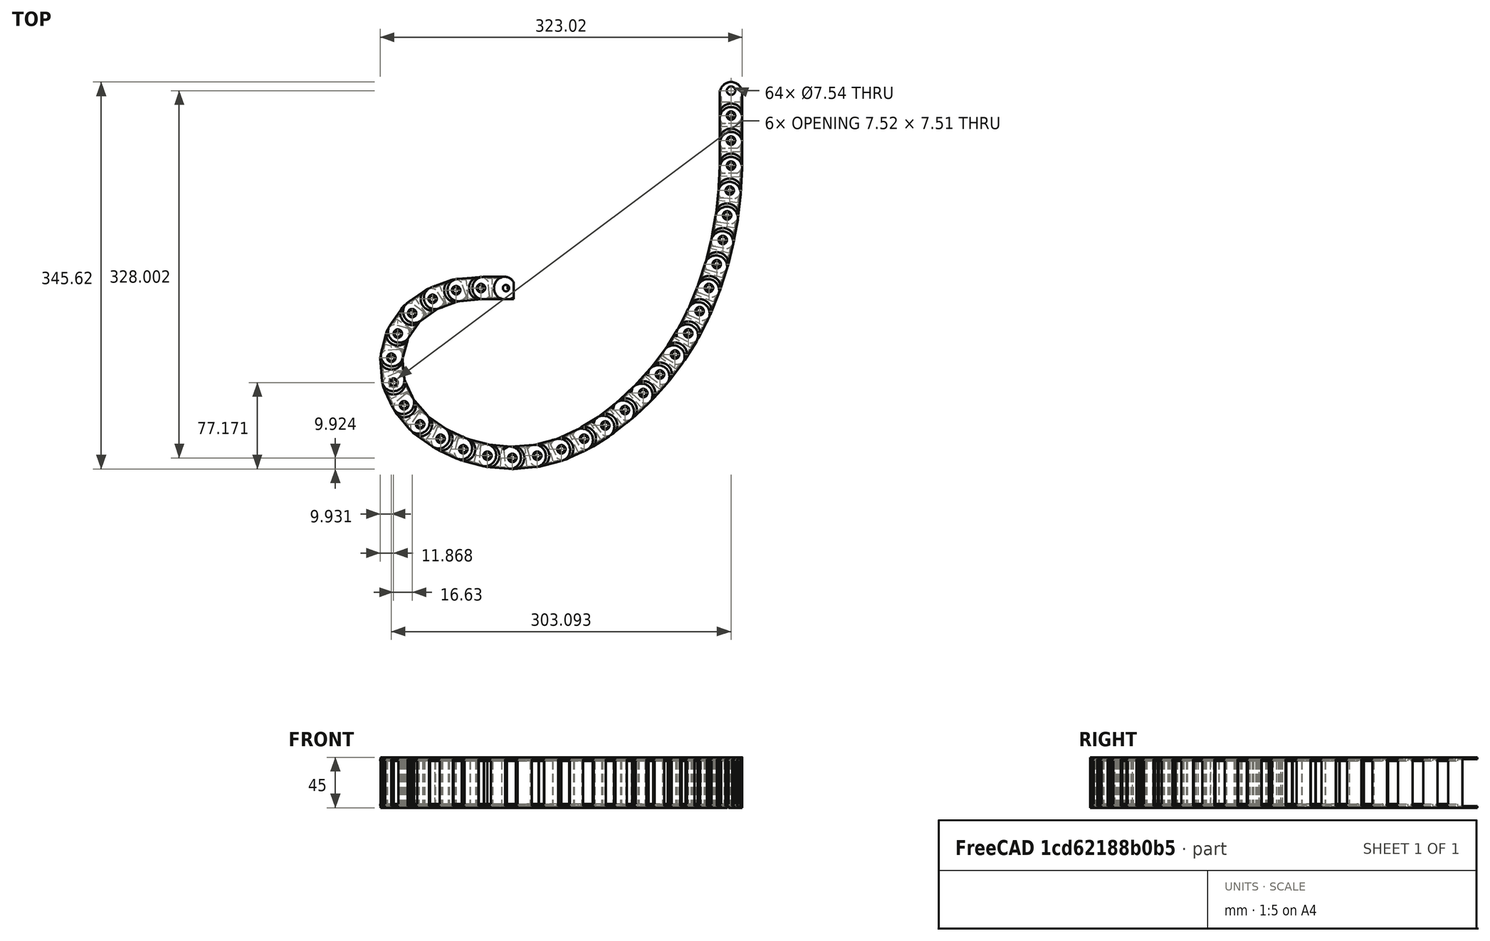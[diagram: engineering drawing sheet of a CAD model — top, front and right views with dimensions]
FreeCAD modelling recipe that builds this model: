
FCSTD DOCUMENT  (FreeCAD 0.16R4945 (Git))
Label: XY-Chain
License: CreativeCommons Attribution-ShareAlike
LicenseURL: http://creativecommons.org/licenses/by-sa/4.0/
objects: Part::Box×320, Part::Cylinder×224, Part::Cut×160, Part::MultiFuse×129, Part::Fuse×96, Part::FeaturePython×1
note: 930 computed .brp shape members not serialized (recipe doc carries the construction recipe); baked Part::Feature solids carry a one-line shape summary decoded from their .brp

FEATURE [Part::Box] cube
  Height = 20
  Length = 26.9231
  Placement = pos=(0,0.1,0) rot=(0,0,1;0rad)
  Width = 45
FEATURE [Part::Cylinder] cylinder
  Angle = 360
  Height = 45
  Placement = pos=(26.9231,0.1,10) rot=(-1,0,0;1.5708rad)
  Radius = 10
FEATURE [Part::Fuse] union
  Base = -> cube
  Tool = -> cylinder
FEATURE [Part::Cylinder] cylinder001
  Angle = 360
  Height = 3
  Placement = pos=(7.07692,2,10) rot=(1,0,0;1.5708rad)
  Radius = 10.5385
FEATURE [Part::Cylinder] cylinder002
  Angle = 360
  Height = 45.9
  Placement = pos=(29.2308,45.5,10) rot=(1,0,0;1.5708rad)
  Radius = 3.76923
FEATURE [Part::Cylinder] cylinder003
  Angle = 360
  Height = 3
  Placement = pos=(7.07692,46.3,10) rot=(1,0,0;1.5708rad)
  Radius = 10.5385
FEATURE [Part::MultiFuse] union001
  Shapes = -> [cylinder001,cylinder002,cylinder003]
FEATURE [Part::Box] cube001
  Height = 6.15385
  Length = 7.69231
  Placement = pos=(0,-0.5,0) rot=(0,0,1;0rad)
  Width = 45.9
FEATURE [Part::Cylinder] cylinder004
  Angle = 360
  Height = 45.9
  Placement = pos=(7.69231,45.4,8.46154) rot=(1,0,0;1.5708rad)
  Radius = 8.46154
FEATURE [Part::Cut] difference
  Base = -> cube001
  Tool = -> cylinder004
FEATURE [Part::Box] cube002
  Height = 6.15385
  Length = 7.69231
  Placement = pos=(0,-0.5,9) rot=(0,0,1;0rad)
  Width = 45.9
FEATURE [Part::Cylinder] cylinder005
  Angle = 360
  Height = 45.9
  Placement = pos=(7.69231,45.4,11.5385) rot=(1,0,0;1.5708rad)
  Radius = 8.46154
FEATURE [Part::Cut] difference001
  Base = -> cube002
  Tool = -> cylinder005
FEATURE [Part::MultiFuse] union002
  Shapes = -> [union001,difference,difference001]
FEATURE [Part::Cut] difference002
  Base = -> union
  Tool = -> union002
FEATURE [Part::Cylinder] cylinder006
  Angle = 360
  Height = 44.2
  Placement = pos=(6.92308,44.7,10) rot=(1,0,0;1.5708rad)
  Radius = 2.84615
FEATURE [Part::Box] cube003
  Height = 4
  Length = 4
  Placement = pos=(0.538462,-2,6.92308) rot=(0,0,-1;0.349066rad)
  Width = 4
FEATURE [Part::Box] cube004
  Height = 4
  Length = 4
  Placement = pos=(0.538462,18.8,6.92308) rot=(0,0,-1;1.22173rad)
  Width = 4
FEATURE [Part::Fuse] union003
  Base = -> cube003
  Tool = -> cube004
FEATURE [Part::Cut] difference003
  Base = -> cylinder006
  Tool = -> union003
FEATURE [Part::Fuse] union004
  Base = -> difference002
  Tool = -> difference003
FEATURE [Part::Box] cube005
  Height = 17
  Length = 40
  Placement = pos=(-1.53846,3.4,1.5) rot=(0,0,1;0rad)
  Width = 38.4
FEATURE [Part::Box] cube006
  Height = 15.3846
  Length = 12.3077
  Placement = pos=(23.6154,3.4,5.38462) rot=(0,0,1;0rad)
  Width = 38.4
FEATURE [Part::Box] cube007
  Height = 24.6154
  Length = 12.3077
  Placement = pos=(-1.53846,3.4,-2.30769) rot=(0,0,1;0rad)
  Width = 38.4
FEATURE [Part::Box] cube008
  Height = 17
  Length = 9.23077
  Placement = pos=(19.2308,1.6,1.5) rot=(0,0,1;0rad)
  Width = 42
FEATURE [Part::Box] cube009
  Height = 20
  Length = 15.3846
  Placement = pos=(23.6154,1.6,0) rot=(0,0,1;0rad)
  Width = 42
FEATURE [Part::MultiFuse] Group
  Shapes = -> [cube007,cube008,cube009]
FEATURE [Part::MultiFuse] union005
  Shapes = -> [cube005,cube006,Group]
FEATURE [Part::Cut] difference004
  Base = -> union004
  Placement = pos=(214.009,254.444,566) rot=(0,-0.707107,0.707107;3.14159rad)
  Tool = -> union005
FEATURE [Part::Box] cube010
  Height = 20
  Length = 26.9231
  Placement = pos=(0,0.1,0) rot=(0,0,1;0rad)
  Width = 45
FEATURE [Part::Cylinder] cylinder007
  Angle = 360
  Height = 45
  Placement = pos=(26.9231,0.1,10) rot=(-1,0,0;1.5708rad)
  Radius = 10
FEATURE [Part::Fuse] union006
  Base = -> cube010
  Tool = -> cylinder007
FEATURE [Part::Cylinder] cylinder008
  Angle = 360
  Height = 3
  Placement = pos=(7.07692,2,10) rot=(1,0,0;1.5708rad)
  Radius = 10.5385
FEATURE [Part::Cylinder] cylinder009
  Angle = 360
  Height = 45.9
  Placement = pos=(29.2308,45.5,10) rot=(1,0,0;1.5708rad)
  Radius = 3.76923
FEATURE [Part::Cylinder] cylinder010
  Angle = 360
  Height = 3
  Placement = pos=(7.07692,46.3,10) rot=(1,0,0;1.5708rad)
  Radius = 10.5385
FEATURE [Part::MultiFuse] union007
  Shapes = -> [cylinder008,cylinder009,cylinder010]
FEATURE [Part::Box] cube011
  Height = 6.15385
  Length = 7.69231
  Placement = pos=(0,-0.5,0) rot=(0,0,1;0rad)
  Width = 45.9
FEATURE [Part::Cylinder] cylinder011
  Angle = 360
  Height = 45.9
  Placement = pos=(7.69231,45.4,8.46154) rot=(1,0,0;1.5708rad)
  Radius = 8.46154
FEATURE [Part::Cut] difference005
  Base = -> cube011
  Tool = -> cylinder011
FEATURE [Part::Box] cube012
  Height = 6.15385
  Length = 7.69231
  Placement = pos=(0,-0.5,9) rot=(0,0,1;0rad)
  Width = 45.9
FEATURE [Part::Cylinder] cylinder012
  Angle = 360
  Height = 45.9
  Placement = pos=(7.69231,45.4,11.5385) rot=(1,0,0;1.5708rad)
  Radius = 8.46154
FEATURE [Part::Cut] difference006
  Base = -> cube012
  Tool = -> cylinder012
FEATURE [Part::MultiFuse] union008
  Shapes = -> [union007,difference005,difference006]
FEATURE [Part::Cut] difference007
  Base = -> union006
  Tool = -> union008
FEATURE [Part::Cylinder] cylinder013
  Angle = 360
  Height = 44.2
  Placement = pos=(6.92308,44.7,10) rot=(1,0,0;1.5708rad)
  Radius = 2.84615
FEATURE [Part::Box] cube013
  Height = 4
  Length = 4
  Placement = pos=(0.538462,-2,6.92308) rot=(0,0,-1;0.349066rad)
  Width = 4
FEATURE [Part::Box] cube014
  Height = 4
  Length = 4
  Placement = pos=(0.538462,18.8,6.92308) rot=(0,0,-1;1.22173rad)
  Width = 4
FEATURE [Part::Fuse] union009
  Base = -> cube013
  Tool = -> cube014
FEATURE [Part::Cut] difference008
  Base = -> cylinder013
  Tool = -> union009
FEATURE [Part::Fuse] union010
  Base = -> difference007
  Tool = -> difference008
FEATURE [Part::Box] cube015
  Height = 17
  Length = 40
  Placement = pos=(-1.53846,3.4,1.5) rot=(0,0,1;0rad)
  Width = 38.4
FEATURE [Part::Box] cube016
  Height = 15.3846
  Length = 12.3077
  Placement = pos=(23.6154,3.4,5.38462) rot=(0,0,1;0rad)
  Width = 38.4
FEATURE [Part::Box] cube017
  Height = 24.6154
  Length = 12.3077
  Placement = pos=(-1.53846,3.4,-2.30769) rot=(0,0,1;0rad)
  Width = 38.4
FEATURE [Part::Box] cube018
  Height = 17
  Length = 9.23077
  Placement = pos=(19.2308,1.6,1.5) rot=(0,0,1;0rad)
  Width = 42
FEATURE [Part::Box] cube019
  Height = 20
  Length = 15.3846
  Placement = pos=(23.6154,1.6,0) rot=(0,0,1;0rad)
  Width = 42
FEATURE [Part::MultiFuse] Group001
  Shapes = -> [cube017,cube018,cube019]
FEATURE [Part::MultiFuse] union011
  Shapes = -> [cube015,cube016,Group001]
FEATURE [Part::Cut] difference009
  Base = -> union010
  Placement = pos=(190.804,255.009,566) rot=(0.030858,-0.70677,0.70677;3.20329rad)
  Tool = -> union011
FEATURE [Part::Box] cube020
  Height = 20
  Length = 26.9231
  Placement = pos=(0,0.1,0) rot=(0,0,1;0rad)
  Width = 45
FEATURE [Part::Cylinder] cylinder014
  Angle = 360
  Height = 45
  Placement = pos=(26.9231,0.1,10) rot=(-1,0,0;1.5708rad)
  Radius = 10
FEATURE [Part::Fuse] union012
  Base = -> cube020
  Tool = -> cylinder014
FEATURE [Part::Cylinder] cylinder015
  Angle = 360
  Height = 3
  Placement = pos=(7.07692,2,10) rot=(1,0,0;1.5708rad)
  Radius = 10.5385
FEATURE [Part::Cylinder] cylinder016
  Angle = 360
  Height = 45.9
  Placement = pos=(29.2308,45.5,10) rot=(1,0,0;1.5708rad)
  Radius = 3.76923
FEATURE [Part::Cylinder] cylinder017
  Angle = 360
  Height = 3
  Placement = pos=(7.07692,46.3,10) rot=(1,0,0;1.5708rad)
  Radius = 10.5385
FEATURE [Part::MultiFuse] union013
  Shapes = -> [cylinder015,cylinder016,cylinder017]
FEATURE [Part::Box] cube021
  Height = 6.15385
  Length = 7.69231
  Placement = pos=(0,-0.5,0) rot=(0,0,1;0rad)
  Width = 45.9
FEATURE [Part::Cylinder] cylinder018
  Angle = 360
  Height = 45.9
  Placement = pos=(7.69231,45.4,8.46154) rot=(1,0,0;1.5708rad)
  Radius = 8.46154
FEATURE [Part::Cut] difference010
  Base = -> cube021
  Tool = -> cylinder018
FEATURE [Part::Box] cube022
  Height = 6.15385
  Length = 7.69231
  Placement = pos=(0,-0.5,9) rot=(0,0,1;0rad)
  Width = 45.9
FEATURE [Part::Cylinder] cylinder019
  Angle = 360
  Height = 45.9
  Placement = pos=(7.69231,45.4,11.5385) rot=(1,0,0;1.5708rad)
  Radius = 8.46154
FEATURE [Part::Cut] difference011
  Base = -> cube022
  Tool = -> cylinder019
FEATURE [Part::MultiFuse] union014
  Shapes = -> [union013,difference010,difference011]
FEATURE [Part::Cut] difference012
  Base = -> union012
  Tool = -> union014
FEATURE [Part::Cylinder] cylinder020
  Angle = 360
  Height = 44.2
  Placement = pos=(6.92308,44.7,10) rot=(1,0,0;1.5708rad)
  Radius = 2.84615
FEATURE [Part::Box] cube023
  Height = 4
  Length = 4
  Placement = pos=(0.538462,-2,6.92308) rot=(0,0,-1;0.349066rad)
  Width = 4
FEATURE [Part::Box] cube024
  Height = 4
  Length = 4
  Placement = pos=(0.538462,18.8,6.92308) rot=(0,0,-1;1.22173rad)
  Width = 4
FEATURE [Part::Fuse] union015
  Base = -> cube023
  Tool = -> cube024
FEATURE [Part::Cut] difference013
  Base = -> cylinder020
  Tool = -> union015
FEATURE [Part::Fuse] union016
  Base = -> difference012
  Tool = -> difference013
FEATURE [Part::Box] cube025
  Height = 17
  Length = 40
  Placement = pos=(-1.53846,3.4,1.5) rot=(0,0,1;0rad)
  Width = 38.4
FEATURE [Part::Box] cube026
  Height = 15.3846
  Length = 12.3077
  Placement = pos=(23.6154,3.4,5.38462) rot=(0,0,1;0rad)
  Width = 38.4
FEATURE [Part::Box] cube027
  Height = 24.6154
  Length = 12.3077
  Placement = pos=(-1.53846,3.4,-2.30769) rot=(0,0,1;0rad)
  Width = 38.4
FEATURE [Part::Box] cube028
  Height = 17
  Length = 9.23077
  Placement = pos=(19.2308,1.6,1.5) rot=(0,0,1;0rad)
  Width = 42
FEATURE [Part::Box] cube029
  Height = 20
  Length = 15.3846
  Placement = pos=(23.6154,1.6,0) rot=(0,0,1;0rad)
  Width = 42
FEATURE [Part::MultiFuse] Group002
  Shapes = -> [cube027,cube028,cube029]
FEATURE [Part::MultiFuse] union017
  Shapes = -> [cube025,cube026,Group002]
FEATURE [Part::Cut] difference014
  Base = -> union016
  Placement = pos=(165.641,254.265,566) rot=(0.123724,-0.701674,0.701674;3.38779rad)
  Tool = -> union017
FEATURE [Part::Box] cube030
  Height = 20
  Length = 26.9231
  Placement = pos=(0,0.1,0) rot=(0,0,1;0rad)
  Width = 45
FEATURE [Part::Cylinder] cylinder021
  Angle = 360
  Height = 45
  Placement = pos=(26.9231,0.1,10) rot=(-1,0,0;1.5708rad)
  Radius = 10
FEATURE [Part::Fuse] union018
  Base = -> cube030
  Tool = -> cylinder021
FEATURE [Part::Cylinder] cylinder022
  Angle = 360
  Height = 3
  Placement = pos=(7.07692,2,10) rot=(1,0,0;1.5708rad)
  Radius = 10.5385
FEATURE [Part::Cylinder] cylinder023
  Angle = 360
  Height = 45.9
  Placement = pos=(29.2308,45.5,10) rot=(1,0,0;1.5708rad)
  Radius = 3.76923
FEATURE [Part::Cylinder] cylinder024
  Angle = 360
  Height = 3
  Placement = pos=(7.07692,46.3,10) rot=(1,0,0;1.5708rad)
  Radius = 10.5385
FEATURE [Part::MultiFuse] union019
  Shapes = -> [cylinder022,cylinder023,cylinder024]
FEATURE [Part::Box] cube031
  Height = 6.15385
  Length = 7.69231
  Placement = pos=(0,-0.5,0) rot=(0,0,1;0rad)
  Width = 45.9
FEATURE [Part::Cylinder] cylinder025
  Angle = 360
  Height = 45.9
  Placement = pos=(7.69231,45.4,8.46154) rot=(1,0,0;1.5708rad)
  Radius = 8.46154
FEATURE [Part::Cut] difference015
  Base = -> cube031
  Tool = -> cylinder025
FEATURE [Part::Box] cube032
  Height = 6.15385
  Length = 7.69231
  Placement = pos=(0,-0.5,9) rot=(0,0,1;0rad)
  Width = 45.9
FEATURE [Part::Cylinder] cylinder026
  Angle = 360
  Height = 45.9
  Placement = pos=(7.69231,45.4,11.5385) rot=(1,0,0;1.5708rad)
  Radius = 8.46154
FEATURE [Part::Cut] difference016
  Base = -> cube032
  Tool = -> cylinder026
FEATURE [Part::MultiFuse] union020
  Shapes = -> [union019,difference015,difference016]
FEATURE [Part::Cut] difference017
  Base = -> union018
  Tool = -> union020
FEATURE [Part::Cylinder] cylinder027
  Angle = 360
  Height = 44.2
  Placement = pos=(6.92308,44.7,10) rot=(1,0,0;1.5708rad)
  Radius = 2.84615
FEATURE [Part::Box] cube033
  Height = 4
  Length = 4
  Placement = pos=(0.538462,-2,6.92308) rot=(0,0,-1;0.349066rad)
  Width = 4
FEATURE [Part::Box] cube034
  Height = 4
  Length = 4
  Placement = pos=(0.538462,18.8,6.92308) rot=(0,0,-1;1.22173rad)
  Width = 4
FEATURE [Part::Fuse] union021
  Base = -> cube033
  Tool = -> cube034
FEATURE [Part::Cut] difference018
  Base = -> cylinder027
  Tool = -> union021
FEATURE [Part::Fuse] union022
  Base = -> difference017
  Tool = -> difference018
FEATURE [Part::Box] cube035
  Height = 17
  Length = 40
  Placement = pos=(-1.53846,3.4,1.5) rot=(0,0,1;0rad)
  Width = 38.4
FEATURE [Part::Box] cube036
  Height = 15.3846
  Length = 12.3077
  Placement = pos=(23.6154,3.4,5.38462) rot=(0,0,1;0rad)
  Width = 38.4
FEATURE [Part::Box] cube037
  Height = 24.6154
  Length = 12.3077
  Placement = pos=(-1.53846,3.4,-2.30769) rot=(0,0,1;0rad)
  Width = 38.4
FEATURE [Part::Box] cube038
  Height = 17
  Length = 9.23077
  Placement = pos=(19.2308,1.6,1.5) rot=(0,0,1;0rad)
  Width = 42
FEATURE [Part::Box] cube039
  Height = 20
  Length = 15.3846
  Placement = pos=(23.6154,1.6,0) rot=(0,0,1;0rad)
  Width = 42
FEATURE [Part::MultiFuse] Group003
  Shapes = -> [cube037,cube038,cube039]
FEATURE [Part::MultiFuse] union023
  Shapes = -> [cube035,cube036,Group003]
FEATURE [Part::Cut] difference019
  Base = -> union022
  Placement = pos=(141.529,247.033,566) rot=(0.217607,-0.690162,0.690162;3.57013rad)
  Tool = -> union023
FEATURE [Part::Box] cube040
  Height = 20
  Length = 26.9231
  Placement = pos=(0,0.1,0) rot=(0,0,1;0rad)
  Width = 45
FEATURE [Part::Cylinder] cylinder028
  Angle = 360
  Height = 45
  Placement = pos=(26.9231,0.1,10) rot=(-1,0,0;1.5708rad)
  Radius = 10
FEATURE [Part::Fuse] union024
  Base = -> cube040
  Tool = -> cylinder028
FEATURE [Part::Cylinder] cylinder029
  Angle = 360
  Height = 3
  Placement = pos=(7.07692,2,10) rot=(1,0,0;1.5708rad)
  Radius = 10.5385
FEATURE [Part::Cylinder] cylinder030
  Angle = 360
  Height = 45.9
  Placement = pos=(29.2308,45.5,10) rot=(1,0,0;1.5708rad)
  Radius = 3.76923
FEATURE [Part::Cylinder] cylinder031
  Angle = 360
  Height = 3
  Placement = pos=(7.07692,46.3,10) rot=(1,0,0;1.5708rad)
  Radius = 10.5385
FEATURE [Part::MultiFuse] union025
  Shapes = -> [cylinder029,cylinder030,cylinder031]
FEATURE [Part::Box] cube041
  Height = 6.15385
  Length = 7.69231
  Placement = pos=(0,-0.5,0) rot=(0,0,1;0rad)
  Width = 45.9
FEATURE [Part::Cylinder] cylinder032
  Angle = 360
  Height = 45.9
  Placement = pos=(7.69231,45.4,8.46154) rot=(1,0,0;1.5708rad)
  Radius = 8.46154
FEATURE [Part::Cut] difference020
  Base = -> cube041
  Tool = -> cylinder032
FEATURE [Part::Box] cube042
  Height = 6.15385
  Length = 7.69231
  Placement = pos=(0,-0.5,9) rot=(0,0,1;0rad)
  Width = 45.9
FEATURE [Part::Cylinder] cylinder033
  Angle = 360
  Height = 45.9
  Placement = pos=(7.69231,45.4,11.5385) rot=(1,0,0;1.5708rad)
  Radius = 8.46154
FEATURE [Part::Cut] difference021
  Base = -> cube042
  Tool = -> cylinder033
FEATURE [Part::MultiFuse] union026
  Shapes = -> [union025,difference020,difference021]
FEATURE [Part::Cut] difference022
  Base = -> union024
  Tool = -> union026
FEATURE [Part::Cylinder] cylinder034
  Angle = 360
  Height = 44.2
  Placement = pos=(6.92308,44.7,10) rot=(1,0,0;1.5708rad)
  Radius = 2.84615
FEATURE [Part::Box] cube043
  Height = 4
  Length = 4
  Placement = pos=(0.538462,-2,6.92308) rot=(0,0,-1;0.349066rad)
  Width = 4
FEATURE [Part::Box] cube044
  Height = 4
  Length = 4
  Placement = pos=(0.538462,18.8,6.92308) rot=(0,0,-1;1.22173rad)
  Width = 4
FEATURE [Part::Fuse] union027
  Base = -> cube043
  Tool = -> cube044
FEATURE [Part::Cut] difference023
  Base = -> cylinder034
  Tool = -> union027
FEATURE [Part::Fuse] union028
  Base = -> difference022
  Tool = -> difference023
FEATURE [Part::Box] cube045
  Height = 17
  Length = 40
  Placement = pos=(-1.53846,3.4,1.5) rot=(0,0,1;0rad)
  Width = 38.4
FEATURE [Part::Box] cube046
  Height = 15.3846
  Length = 12.3077
  Placement = pos=(23.6154,3.4,5.38462) rot=(0,0,1;0rad)
  Width = 38.4
FEATURE [Part::Box] cube047
  Height = 24.6154
  Length = 12.3077
  Placement = pos=(-1.53846,3.4,-2.30769) rot=(0,0,1;0rad)
  Width = 38.4
FEATURE [Part::Box] cube048
  Height = 17
  Length = 9.23077
  Placement = pos=(19.2308,1.6,1.5) rot=(0,0,1;0rad)
  Width = 42
FEATURE [Part::Box] cube049
  Height = 20
  Length = 15.3846
  Placement = pos=(23.6154,1.6,0) rot=(0,0,1;0rad)
  Width = 42
FEATURE [Part::MultiFuse] Group004
  Shapes = -> [cube047,cube048,cube049]
FEATURE [Part::MultiFuse] union029
  Shapes = -> [cube045,cube046,Group004]
FEATURE [Part::Cut] difference024
  Base = -> union028
  Placement = pos=(119.099,233.482,566) rot=(0.345437,-0.663579,0.663579;3.8068rad)
  Tool = -> union029
FEATURE [Part::Box] cube050
  Height = 20
  Length = 26.9231
  Placement = pos=(0,0.1,0) rot=(0,0,1;0rad)
  Width = 45
FEATURE [Part::Cylinder] cylinder035
  Angle = 360
  Height = 45
  Placement = pos=(26.9231,0.1,10) rot=(-1,0,0;1.5708rad)
  Radius = 10
FEATURE [Part::Fuse] union030
  Base = -> cube050
  Tool = -> cylinder035
FEATURE [Part::Cylinder] cylinder036
  Angle = 360
  Height = 3
  Placement = pos=(7.07692,2,10) rot=(1,0,0;1.5708rad)
  Radius = 10.5385
FEATURE [Part::Cylinder] cylinder037
  Angle = 360
  Height = 45.9
  Placement = pos=(29.2308,45.5,10) rot=(1,0,0;1.5708rad)
  Radius = 3.76923
FEATURE [Part::Cylinder] cylinder038
  Angle = 360
  Height = 3
  Placement = pos=(7.07692,46.3,10) rot=(1,0,0;1.5708rad)
  Radius = 10.5385
FEATURE [Part::MultiFuse] union031
  Shapes = -> [cylinder036,cylinder037,cylinder038]
FEATURE [Part::Box] cube051
  Height = 6.15385
  Length = 7.69231
  Placement = pos=(0,-0.5,0) rot=(0,0,1;0rad)
  Width = 45.9
FEATURE [Part::Cylinder] cylinder039
  Angle = 360
  Height = 45.9
  Placement = pos=(7.69231,45.4,8.46154) rot=(1,0,0;1.5708rad)
  Radius = 8.46154
FEATURE [Part::Cut] difference025
  Base = -> cube051
  Tool = -> cylinder039
FEATURE [Part::Box] cube052
  Height = 6.15385
  Length = 7.69231
  Placement = pos=(0,-0.5,9) rot=(0,0,1;0rad)
  Width = 45.9
FEATURE [Part::Cylinder] cylinder040
  Angle = 360
  Height = 45.9
  Placement = pos=(7.69231,45.4,11.5385) rot=(1,0,0;1.5708rad)
  Radius = 8.46154
FEATURE [Part::Cut] difference026
  Base = -> cube052
  Tool = -> cylinder040
FEATURE [Part::MultiFuse] union032
  Shapes = -> [union031,difference025,difference026]
FEATURE [Part::Cut] difference027
  Base = -> union030
  Tool = -> union032
FEATURE [Part::Cylinder] cylinder041
  Angle = 360
  Height = 44.2
  Placement = pos=(6.92308,44.7,10) rot=(1,0,0;1.5708rad)
  Radius = 2.84615
FEATURE [Part::Box] cube053
  Height = 4
  Length = 4
  Placement = pos=(0.538462,-2,6.92308) rot=(0,0,-1;0.349066rad)
  Width = 4
FEATURE [Part::Box] cube054
  Height = 4
  Length = 4
  Placement = pos=(0.538462,18.8,6.92308) rot=(0,0,-1;1.22173rad)
  Width = 4
FEATURE [Part::Fuse] union033
  Base = -> cube053
  Tool = -> cube054
FEATURE [Part::Cut] difference028
  Base = -> cylinder041
  Tool = -> union033
FEATURE [Part::Fuse] union034
  Base = -> difference027
  Tool = -> difference028
FEATURE [Part::Box] cube055
  Height = 17
  Length = 40
  Placement = pos=(-1.53846,3.4,1.5) rot=(0,0,1;0rad)
  Width = 38.4
FEATURE [Part::Box] cube056
  Height = 15.3846
  Length = 12.3077
  Placement = pos=(23.6154,3.4,5.38462) rot=(0,0,1;0rad)
  Width = 38.4
FEATURE [Part::Box] cube057
  Height = 24.6154
  Length = 12.3077
  Placement = pos=(-1.53846,3.4,-2.30769) rot=(0,0,1;0rad)
  Width = 38.4
FEATURE [Part::Box] cube058
  Height = 17
  Length = 9.23077
  Placement = pos=(19.2308,1.6,1.5) rot=(0,0,1;0rad)
  Width = 42
FEATURE [Part::Box] cube059
  Height = 20
  Length = 15.3846
  Placement = pos=(23.6154,1.6,0) rot=(0,0,1;0rad)
  Width = 42
FEATURE [Part::MultiFuse] Group005
  Shapes = -> [cube057,cube058,cube059]
FEATURE [Part::MultiFuse] union035
  Shapes = -> [cube055,cube056,Group005]
FEATURE [Part::Cut] difference029
  Base = -> union034
  Placement = pos=(102.657,213.077,566) rot=(0.476905,-0.621515,0.621515;4.0316rad)
  Tool = -> union035
FEATURE [Part::Box] cube060
  Height = 20
  Length = 26.9231
  Placement = pos=(0,0.1,0) rot=(0,0,1;0rad)
  Width = 45
FEATURE [Part::Cylinder] cylinder042
  Angle = 360
  Height = 45
  Placement = pos=(26.9231,0.1,10) rot=(-1,0,0;1.5708rad)
  Radius = 10
FEATURE [Part::Fuse] union036
  Base = -> cube060
  Tool = -> cylinder042
FEATURE [Part::Cylinder] cylinder043
  Angle = 360
  Height = 3
  Placement = pos=(7.07692,2,10) rot=(1,0,0;1.5708rad)
  Radius = 10.5385
FEATURE [Part::Cylinder] cylinder044
  Angle = 360
  Height = 45.9
  Placement = pos=(29.2308,45.5,10) rot=(1,0,0;1.5708rad)
  Radius = 3.76923
FEATURE [Part::Cylinder] cylinder045
  Angle = 360
  Height = 3
  Placement = pos=(7.07692,46.3,10) rot=(1,0,0;1.5708rad)
  Radius = 10.5385
FEATURE [Part::MultiFuse] union037
  Shapes = -> [cylinder043,cylinder044,cylinder045]
FEATURE [Part::Box] cube061
  Height = 6.15385
  Length = 7.69231
  Placement = pos=(0,-0.5,0) rot=(0,0,1;0rad)
  Width = 45.9
FEATURE [Part::Cylinder] cylinder046
  Angle = 360
  Height = 45.9
  Placement = pos=(7.69231,45.4,8.46154) rot=(1,0,0;1.5708rad)
  Radius = 8.46154
FEATURE [Part::Cut] difference030
  Base = -> cube061
  Tool = -> cylinder046
FEATURE [Part::Box] cube062
  Height = 6.15385
  Length = 7.69231
  Placement = pos=(0,-0.5,9) rot=(0,0,1;0rad)
  Width = 45.9
FEATURE [Part::Cylinder] cylinder047
  Angle = 360
  Height = 45.9
  Placement = pos=(7.69231,45.4,11.5385) rot=(1,0,0;1.5708rad)
  Radius = 8.46154
FEATURE [Part::Cut] difference031
  Base = -> cube062
  Tool = -> cylinder047
FEATURE [Part::MultiFuse] union038
  Shapes = -> [union037,difference030,difference031]
FEATURE [Part::Cut] difference032
  Base = -> union036
  Tool = -> union038
FEATURE [Part::Cylinder] cylinder048
  Angle = 360
  Height = 44.2
  Placement = pos=(6.92308,44.7,10) rot=(1,0,0;1.5708rad)
  Radius = 2.84615
FEATURE [Part::Box] cube063
  Height = 4
  Length = 4
  Placement = pos=(0.538462,-2,6.92308) rot=(0,0,-1;0.349066rad)
  Width = 4
FEATURE [Part::Box] cube064
  Height = 4
  Length = 4
  Placement = pos=(0.538462,18.8,6.92308) rot=(0,0,-1;1.22173rad)
  Width = 4
FEATURE [Part::Fuse] union039
  Base = -> cube063
  Tool = -> cube064
FEATURE [Part::Cut] difference033
  Base = -> cylinder048
  Tool = -> union039
FEATURE [Part::Fuse] union040
  Base = -> difference032
  Tool = -> difference033
FEATURE [Part::Box] cube065
  Height = 17
  Length = 40
  Placement = pos=(-1.53846,3.4,1.5) rot=(0,0,1;0rad)
  Width = 38.4
FEATURE [Part::Box] cube066
  Height = 15.3846
  Length = 12.3077
  Placement = pos=(23.6154,3.4,5.38462) rot=(0,0,1;0rad)
  Width = 38.4
FEATURE [Part::Box] cube067
  Height = 24.6154
  Length = 12.3077
  Placement = pos=(-1.53846,3.4,-2.30769) rot=(0,0,1;0rad)
  Width = 38.4
FEATURE [Part::Box] cube068
  Height = 17
  Length = 9.23077
  Placement = pos=(19.2308,1.6,1.5) rot=(0,0,1;0rad)
  Width = 42
FEATURE [Part::Box] cube069
  Height = 20
  Length = 15.3846
  Placement = pos=(23.6154,1.6,0) rot=(0,0,1;0rad)
  Width = 42
FEATURE [Part::MultiFuse] Group006
  Shapes = -> [cube067,cube068,cube069]
FEATURE [Part::MultiFuse] union041
  Shapes = -> [cube065,cube066,Group006]
FEATURE [Part::Cut] difference034
  Base = -> union040
  Placement = pos=(94.1856,188.279,566) rot=(0.610924,-0.559809,0.559809;4.23842rad)
  Tool = -> union041
FEATURE [Part::Box] cube070
  Height = 20
  Length = 26.9231
  Placement = pos=(0,0.1,0) rot=(0,0,1;0rad)
  Width = 45
FEATURE [Part::Cylinder] cylinder049
  Angle = 360
  Height = 45
  Placement = pos=(26.9231,0.1,10) rot=(-1,0,0;1.5708rad)
  Radius = 10
FEATURE [Part::Fuse] union042
  Base = -> cube070
  Tool = -> cylinder049
FEATURE [Part::Cylinder] cylinder050
  Angle = 360
  Height = 3
  Placement = pos=(7.07692,2,10) rot=(1,0,0;1.5708rad)
  Radius = 10.5385
FEATURE [Part::Cylinder] cylinder051
  Angle = 360
  Height = 45.9
  Placement = pos=(29.2308,45.5,10) rot=(1,0,0;1.5708rad)
  Radius = 3.76923
FEATURE [Part::Cylinder] cylinder052
  Angle = 360
  Height = 3
  Placement = pos=(7.07692,46.3,10) rot=(1,0,0;1.5708rad)
  Radius = 10.5385
FEATURE [Part::MultiFuse] union043
  Shapes = -> [cylinder050,cylinder051,cylinder052]
FEATURE [Part::Box] cube071
  Height = 6.15385
  Length = 7.69231
  Placement = pos=(0,-0.5,0) rot=(0,0,1;0rad)
  Width = 45.9
FEATURE [Part::Cylinder] cylinder053
  Angle = 360
  Height = 45.9
  Placement = pos=(7.69231,45.4,8.46154) rot=(1,0,0;1.5708rad)
  Radius = 8.46154
FEATURE [Part::Cut] difference035
  Base = -> cube071
  Tool = -> cylinder053
FEATURE [Part::Box] cube072
  Height = 6.15385
  Length = 7.69231
  Placement = pos=(0,-0.5,9) rot=(0,0,1;0rad)
  Width = 45.9
FEATURE [Part::Cylinder] cylinder054
  Angle = 360
  Height = 45.9
  Placement = pos=(7.69231,45.4,11.5385) rot=(1,0,0;1.5708rad)
  Radius = 8.46154
FEATURE [Part::Cut] difference036
  Base = -> cube072
  Tool = -> cylinder054
FEATURE [Part::MultiFuse] union044
  Shapes = -> [union043,difference035,difference036]
FEATURE [Part::Cut] difference037
  Base = -> union042
  Tool = -> union044
FEATURE [Part::Cylinder] cylinder055
  Angle = 360
  Height = 44.2
  Placement = pos=(6.92308,44.7,10) rot=(1,0,0;1.5708rad)
  Radius = 2.84615
FEATURE [Part::Box] cube073
  Height = 4
  Length = 4
  Placement = pos=(0.538462,-2,6.92308) rot=(0,0,-1;0.349066rad)
  Width = 4
FEATURE [Part::Box] cube074
  Height = 4
  Length = 4
  Placement = pos=(0.538462,18.8,6.92308) rot=(0,0,-1;1.22173rad)
  Width = 4
FEATURE [Part::Fuse] union045
  Base = -> cube073
  Tool = -> cube074
FEATURE [Part::Cut] difference038
  Base = -> cylinder055
  Tool = -> union045
FEATURE [Part::Fuse] union046
  Base = -> difference037
  Tool = -> difference038
FEATURE [Part::Box] cube075
  Height = 17
  Length = 40
  Placement = pos=(-1.53846,3.4,1.5) rot=(0,0,1;0rad)
  Width = 38.4
FEATURE [Part::Box] cube076
  Height = 15.3846
  Length = 12.3077
  Placement = pos=(23.6154,3.4,5.38462) rot=(0,0,1;0rad)
  Width = 38.4
FEATURE [Part::Box] cube077
  Height = 24.6154
  Length = 12.3077
  Placement = pos=(-1.53846,3.4,-2.30769) rot=(0,0,1;0rad)
  Width = 38.4
FEATURE [Part::Box] cube078
  Height = 17
  Length = 9.23077
  Placement = pos=(19.2308,1.6,1.5) rot=(0,0,1;0rad)
  Width = 42
FEATURE [Part::Box] cube079
  Height = 20
  Length = 15.3846
  Placement = pos=(23.6154,1.6,0) rot=(0,0,1;0rad)
  Width = 42
FEATURE [Part::MultiFuse] Group007
  Shapes = -> [cube077,cube078,cube079]
FEATURE [Part::MultiFuse] union047
  Shapes = -> [cube075,cube076,Group007]
FEATURE [Part::Cut] difference039
  Base = -> union046
  Placement = pos=(94.706,162.079,566) rot=(0.742942,-0.473306,0.473306;4.41953rad)
  Tool = -> union047
FEATURE [Part::Box] cube080
  Height = 20
  Length = 26.9231
  Placement = pos=(0,0.1,0) rot=(0,0,1;0rad)
  Width = 45
FEATURE [Part::Cylinder] cylinder056
  Angle = 360
  Height = 45
  Placement = pos=(26.9231,0.1,10) rot=(-1,0,0;1.5708rad)
  Radius = 10
FEATURE [Part::Fuse] union048
  Base = -> cube080
  Tool = -> cylinder056
FEATURE [Part::Cylinder] cylinder057
  Angle = 360
  Height = 3
  Placement = pos=(7.07692,2,10) rot=(1,0,0;1.5708rad)
  Radius = 10.5385
FEATURE [Part::Cylinder] cylinder058
  Angle = 360
  Height = 45.9
  Placement = pos=(29.2308,45.5,10) rot=(1,0,0;1.5708rad)
  Radius = 3.76923
FEATURE [Part::Cylinder] cylinder059
  Angle = 360
  Height = 3
  Placement = pos=(7.07692,46.3,10) rot=(1,0,0;1.5708rad)
  Radius = 10.5385
FEATURE [Part::MultiFuse] union049
  Shapes = -> [cylinder057,cylinder058,cylinder059]
FEATURE [Part::Box] cube081
  Height = 6.15385
  Length = 7.69231
  Placement = pos=(0,-0.5,0) rot=(0,0,1;0rad)
  Width = 45.9
FEATURE [Part::Cylinder] cylinder060
  Angle = 360
  Height = 45.9
  Placement = pos=(7.69231,45.4,8.46154) rot=(1,0,0;1.5708rad)
  Radius = 8.46154
FEATURE [Part::Cut] difference040
  Base = -> cube081
  Tool = -> cylinder060
FEATURE [Part::Box] cube082
  Height = 6.15385
  Length = 7.69231
  Placement = pos=(0,-0.5,9) rot=(0,0,1;0rad)
  Width = 45.9
FEATURE [Part::Cylinder] cylinder061
  Angle = 360
  Height = 45.9
  Placement = pos=(7.69231,45.4,11.5385) rot=(1,0,0;1.5708rad)
  Radius = 8.46154
FEATURE [Part::Cut] difference041
  Base = -> cube082
  Tool = -> cylinder061
FEATURE [Part::MultiFuse] union050
  Shapes = -> [union049,difference040,difference041]
FEATURE [Part::Cut] difference042
  Base = -> union048
  Tool = -> union050
FEATURE [Part::Cylinder] cylinder062
  Angle = 360
  Height = 44.2
  Placement = pos=(6.92308,44.7,10) rot=(1,0,0;1.5708rad)
  Radius = 2.84615
FEATURE [Part::Box] cube083
  Height = 4
  Length = 4
  Placement = pos=(0.538462,-2,6.92308) rot=(0,0,-1;0.349066rad)
  Width = 4
FEATURE [Part::Box] cube084
  Height = 4
  Length = 4
  Placement = pos=(0.538462,18.8,6.92308) rot=(0,0,-1;1.22173rad)
  Width = 4
FEATURE [Part::Fuse] union051
  Base = -> cube083
  Tool = -> cube084
FEATURE [Part::Cut] difference043
  Base = -> cylinder062
  Tool = -> union051
FEATURE [Part::Fuse] union052
  Base = -> difference042
  Tool = -> difference043
FEATURE [Part::Box] cube085
  Height = 17
  Length = 40
  Placement = pos=(-1.53846,3.4,1.5) rot=(0,0,1;0rad)
  Width = 38.4
FEATURE [Part::Box] cube086
  Height = 15.3846
  Length = 12.3077
  Placement = pos=(23.6154,3.4,5.38462) rot=(0,0,1;0rad)
  Width = 38.4
FEATURE [Part::Box] cube087
  Height = 24.6154
  Length = 12.3077
  Placement = pos=(-1.53846,3.4,-2.30769) rot=(0,0,1;0rad)
  Width = 38.4
FEATURE [Part::Box] cube088
  Height = 17
  Length = 9.23077
  Placement = pos=(19.2308,1.6,1.5) rot=(0,0,1;0rad)
  Width = 42
FEATURE [Part::Box] cube089
  Height = 20
  Length = 15.3846
  Placement = pos=(23.6154,1.6,0) rot=(0,0,1;0rad)
  Width = 42
FEATURE [Part::MultiFuse] Group008
  Shapes = -> [cube087,cube088,cube089]
FEATURE [Part::MultiFuse] union053
  Shapes = -> [cube085,cube086,Group008]
FEATURE [Part::Cut] difference044
  Base = -> union052
  Placement = pos=(104.012,138.69,566) rot=(0.834817,-0.389282,0.389282;4.53282rad)
  Tool = -> union053
FEATURE [Part::Box] cube090
  Height = 20
  Length = 26.9231
  Placement = pos=(0,0.1,0) rot=(0,0,1;0rad)
  Width = 45
FEATURE [Part::Cylinder] cylinder063
  Angle = 360
  Height = 45
  Placement = pos=(26.9231,0.1,10) rot=(-1,0,0;1.5708rad)
  Radius = 10
FEATURE [Part::Fuse] union054
  Base = -> cube090
  Tool = -> cylinder063
FEATURE [Part::Cylinder] cylinder064
  Angle = 360
  Height = 3
  Placement = pos=(7.07692,2,10) rot=(1,0,0;1.5708rad)
  Radius = 10.5385
FEATURE [Part::Cylinder] cylinder065
  Angle = 360
  Height = 45.9
  Placement = pos=(29.2308,45.5,10) rot=(1,0,0;1.5708rad)
  Radius = 3.76923
FEATURE [Part::Cylinder] cylinder066
  Angle = 360
  Height = 3
  Placement = pos=(7.07692,46.3,10) rot=(1,0,0;1.5708rad)
  Radius = 10.5385
FEATURE [Part::MultiFuse] union055
  Shapes = -> [cylinder064,cylinder065,cylinder066]
FEATURE [Part::Box] cube091
  Height = 6.15385
  Length = 7.69231
  Placement = pos=(0,-0.5,0) rot=(0,0,1;0rad)
  Width = 45.9
FEATURE [Part::Cylinder] cylinder067
  Angle = 360
  Height = 45.9
  Placement = pos=(7.69231,45.4,8.46154) rot=(1,0,0;1.5708rad)
  Radius = 8.46154
FEATURE [Part::Cut] difference045
  Base = -> cube091
  Tool = -> cylinder067
FEATURE [Part::Box] cube092
  Height = 6.15385
  Length = 7.69231
  Placement = pos=(0,-0.5,9) rot=(0,0,1;0rad)
  Width = 45.9
FEATURE [Part::Cylinder] cylinder068
  Angle = 360
  Height = 45.9
  Placement = pos=(7.69231,45.4,11.5385) rot=(1,0,0;1.5708rad)
  Radius = 8.46154
FEATURE [Part::Cut] difference046
  Base = -> cube092
  Tool = -> cylinder068
FEATURE [Part::MultiFuse] union056
  Shapes = -> [union055,difference045,difference046]
FEATURE [Part::Cut] difference047
  Base = -> union054
  Tool = -> union056
FEATURE [Part::Cylinder] cylinder069
  Angle = 360
  Height = 44.2
  Placement = pos=(6.92308,44.7,10) rot=(1,0,0;1.5708rad)
  Radius = 2.84615
FEATURE [Part::Box] cube093
  Height = 4
  Length = 4
  Placement = pos=(0.538462,-2,6.92308) rot=(0,0,-1;0.349066rad)
  Width = 4
FEATURE [Part::Box] cube094
  Height = 4
  Length = 4
  Placement = pos=(0.538462,18.8,6.92308) rot=(0,0,-1;1.22173rad)
  Width = 4
FEATURE [Part::Fuse] union057
  Base = -> cube093
  Tool = -> cube094
FEATURE [Part::Cut] difference048
  Base = -> cylinder069
  Tool = -> union057
FEATURE [Part::Fuse] union058
  Base = -> difference047
  Tool = -> difference048
FEATURE [Part::Box] cube095
  Height = 17
  Length = 40
  Placement = pos=(-1.53846,3.4,1.5) rot=(0,0,1;0rad)
  Width = 38.4
FEATURE [Part::Box] cube096
  Height = 15.3846
  Length = 12.3077
  Placement = pos=(23.6154,3.4,5.38462) rot=(0,0,1;0rad)
  Width = 38.4
FEATURE [Part::Box] cube097
  Height = 24.6154
  Length = 12.3077
  Placement = pos=(-1.53846,3.4,-2.30769) rot=(0,0,1;0rad)
  Width = 38.4
FEATURE [Part::Box] cube098
  Height = 17
  Length = 9.23077
  Placement = pos=(19.2308,1.6,1.5) rot=(0,0,1;0rad)
  Width = 42
FEATURE [Part::Box] cube099
  Height = 20
  Length = 15.3846
  Placement = pos=(23.6154,1.6,0) rot=(0,0,1;0rad)
  Width = 42
FEATURE [Part::MultiFuse] Group009
  Shapes = -> [cube097,cube098,cube099]
FEATURE [Part::MultiFuse] union059
  Shapes = -> [cube095,cube096,Group009]
FEATURE [Part::Cut] difference049
  Base = -> union058
  Placement = pos=(119.055,118.504,566) rot=(0.913318,-0.287968,0.287968;4.62184rad)
  Tool = -> union059
FEATURE [Part::Box] cube100
  Height = 20
  Length = 26.9231
  Placement = pos=(0,0.1,0) rot=(0,0,1;0rad)
  Width = 45
FEATURE [Part::Cylinder] cylinder070
  Angle = 360
  Height = 45
  Placement = pos=(26.9231,0.1,10) rot=(-1,0,0;1.5708rad)
  Radius = 10
FEATURE [Part::Fuse] union060
  Base = -> cube100
  Tool = -> cylinder070
FEATURE [Part::Cylinder] cylinder071
  Angle = 360
  Height = 3
  Placement = pos=(7.07692,2,10) rot=(1,0,0;1.5708rad)
  Radius = 10.5385
FEATURE [Part::Cylinder] cylinder072
  Angle = 360
  Height = 45.9
  Placement = pos=(29.2308,45.5,10) rot=(1,0,0;1.5708rad)
  Radius = 3.76923
FEATURE [Part::Cylinder] cylinder073
  Angle = 360
  Height = 3
  Placement = pos=(7.07692,46.3,10) rot=(1,0,0;1.5708rad)
  Radius = 10.5385
FEATURE [Part::MultiFuse] union061
  Shapes = -> [cylinder071,cylinder072,cylinder073]
FEATURE [Part::Box] cube101
  Height = 6.15385
  Length = 7.69231
  Placement = pos=(0,-0.5,0) rot=(0,0,1;0rad)
  Width = 45.9
FEATURE [Part::Cylinder] cylinder074
  Angle = 360
  Height = 45.9
  Placement = pos=(7.69231,45.4,8.46154) rot=(1,0,0;1.5708rad)
  Radius = 8.46154
FEATURE [Part::Cut] difference050
  Base = -> cube101
  Tool = -> cylinder074
FEATURE [Part::Box] cube102
  Height = 6.15385
  Length = 7.69231
  Placement = pos=(0,-0.5,9) rot=(0,0,1;0rad)
  Width = 45.9
FEATURE [Part::Cylinder] cylinder075
  Angle = 360
  Height = 45.9
  Placement = pos=(7.69231,45.4,11.5385) rot=(1,0,0;1.5708rad)
  Radius = 8.46154
FEATURE [Part::Cut] difference051
  Base = -> cube102
  Tool = -> cylinder075
FEATURE [Part::MultiFuse] union062
  Shapes = -> [union061,difference050,difference051]
FEATURE [Part::Cut] difference052
  Base = -> union060
  Tool = -> union062
FEATURE [Part::Cylinder] cylinder076
  Angle = 360
  Height = 44.2
  Placement = pos=(6.92308,44.7,10) rot=(1,0,0;1.5708rad)
  Radius = 2.84615
FEATURE [Part::Box] cube103
  Height = 4
  Length = 4
  Placement = pos=(0.538462,-2,6.92308) rot=(0,0,-1;0.349066rad)
  Width = 4
FEATURE [Part::Box] cube104
  Height = 4
  Length = 4
  Placement = pos=(0.538462,18.8,6.92308) rot=(0,0,-1;1.22173rad)
  Width = 4
FEATURE [Part::Fuse] union063
  Base = -> cube103
  Tool = -> cube104
FEATURE [Part::Cut] difference053
  Base = -> cylinder076
  Tool = -> union063
FEATURE [Part::Fuse] union064
  Base = -> difference052
  Tool = -> difference053
FEATURE [Part::Box] cube105
  Height = 17
  Length = 40
  Placement = pos=(-1.53846,3.4,1.5) rot=(0,0,1;0rad)
  Width = 38.4
FEATURE [Part::Box] cube106
  Height = 15.3846
  Length = 12.3077
  Placement = pos=(23.6154,3.4,5.38462) rot=(0,0,1;0rad)
  Width = 38.4
FEATURE [Part::Box] cube107
  Height = 24.6154
  Length = 12.3077
  Placement = pos=(-1.53846,3.4,-2.30769) rot=(0,0,1;0rad)
  Width = 38.4
FEATURE [Part::Box] cube108
  Height = 17
  Length = 9.23077
  Placement = pos=(19.2308,1.6,1.5) rot=(0,0,1;0rad)
  Width = 42
FEATURE [Part::Box] cube109
  Height = 20
  Length = 15.3846
  Placement = pos=(23.6154,1.6,0) rot=(0,0,1;0rad)
  Width = 42
FEATURE [Part::MultiFuse] Group010
  Shapes = -> [cube107,cube108,cube109]
FEATURE [Part::MultiFuse] union065
  Shapes = -> [cube105,cube106,Group010]
FEATURE [Part::Cut] difference054
  Base = -> union064
  Placement = pos=(138.235,103.793,566) rot=(0.954201,-0.211541,0.211541;4.66553rad)
  Tool = -> union065
FEATURE [Part::Box] cube110
  Height = 20
  Length = 26.9231
  Placement = pos=(0,0.1,0) rot=(0,0,1;0rad)
  Width = 45
FEATURE [Part::Cylinder] cylinder077
  Angle = 360
  Height = 45
  Placement = pos=(26.9231,0.1,10) rot=(-1,0,0;1.5708rad)
  Radius = 10
FEATURE [Part::Fuse] union066
  Base = -> cube110
  Tool = -> cylinder077
FEATURE [Part::Cylinder] cylinder078
  Angle = 360
  Height = 3
  Placement = pos=(7.07692,2,10) rot=(1,0,0;1.5708rad)
  Radius = 10.5385
FEATURE [Part::Cylinder] cylinder079
  Angle = 360
  Height = 45.9
  Placement = pos=(29.2308,45.5,10) rot=(1,0,0;1.5708rad)
  Radius = 3.76923
FEATURE [Part::Cylinder] cylinder080
  Angle = 360
  Height = 3
  Placement = pos=(7.07692,46.3,10) rot=(1,0,0;1.5708rad)
  Radius = 10.5385
FEATURE [Part::MultiFuse] union067
  Shapes = -> [cylinder078,cylinder079,cylinder080]
FEATURE [Part::Box] cube111
  Height = 6.15385
  Length = 7.69231
  Placement = pos=(0,-0.5,0) rot=(0,0,1;0rad)
  Width = 45.9
FEATURE [Part::Cylinder] cylinder081
  Angle = 360
  Height = 45.9
  Placement = pos=(7.69231,45.4,8.46154) rot=(1,0,0;1.5708rad)
  Radius = 8.46154
FEATURE [Part::Cut] difference055
  Base = -> cube111
  Tool = -> cylinder081
FEATURE [Part::Box] cube112
  Height = 6.15385
  Length = 7.69231
  Placement = pos=(0,-0.5,9) rot=(0,0,1;0rad)
  Width = 45.9
FEATURE [Part::Cylinder] cylinder082
  Angle = 360
  Height = 45.9
  Placement = pos=(7.69231,45.4,11.5385) rot=(1,0,0;1.5708rad)
  Radius = 8.46154
FEATURE [Part::Cut] difference056
  Base = -> cube112
  Tool = -> cylinder082
FEATURE [Part::MultiFuse] union068
  Shapes = -> [union067,difference055,difference056]
FEATURE [Part::Cut] difference057
  Base = -> union066
  Tool = -> union068
FEATURE [Part::Cylinder] cylinder083
  Angle = 360
  Height = 44.2
  Placement = pos=(6.92308,44.7,10) rot=(1,0,0;1.5708rad)
  Radius = 2.84615
FEATURE [Part::Box] cube113
  Height = 4
  Length = 4
  Placement = pos=(0.538462,-2,6.92308) rot=(0,0,-1;0.349066rad)
  Width = 4
FEATURE [Part::Box] cube114
  Height = 4
  Length = 4
  Placement = pos=(0.538462,18.8,6.92308) rot=(0,0,-1;1.22173rad)
  Width = 4
FEATURE [Part::Fuse] union069
  Base = -> cube113
  Tool = -> cube114
FEATURE [Part::Cut] difference058
  Base = -> cylinder083
  Tool = -> union069
FEATURE [Part::Fuse] union070
  Base = -> difference057
  Tool = -> difference058
FEATURE [Part::Box] cube115
  Height = 17
  Length = 40
  Placement = pos=(-1.53846,3.4,1.5) rot=(0,0,1;0rad)
  Width = 38.4
FEATURE [Part::Box] cube116
  Height = 15.3846
  Length = 12.3077
  Placement = pos=(23.6154,3.4,5.38462) rot=(0,0,1;0rad)
  Width = 38.4
FEATURE [Part::Box] cube117
  Height = 24.6154
  Length = 12.3077
  Placement = pos=(-1.53846,3.4,-2.30769) rot=(0,0,1;0rad)
  Width = 38.4
FEATURE [Part::Box] cube118
  Height = 17
  Length = 9.23077
  Placement = pos=(19.2308,1.6,1.5) rot=(0,0,1;0rad)
  Width = 42
FEATURE [Part::Box] cube119
  Height = 20
  Length = 15.3846
  Placement = pos=(23.6154,1.6,0) rot=(0,0,1;0rad)
  Width = 42
FEATURE [Part::MultiFuse] Group011
  Shapes = -> [cube117,cube118,cube119]
FEATURE [Part::MultiFuse] union071
  Shapes = -> [cube115,cube116,Group011]
FEATURE [Part::Cut] difference059
  Base = -> union070
  Placement = pos=(159.678,92.6346,566) rot=(0.983106,-0.129428,0.129428;4.69535rad)
  Tool = -> union071
FEATURE [Part::Box] cube120
  Height = 20
  Length = 26.9231
  Placement = pos=(0,0.1,0) rot=(0,0,1;0rad)
  Width = 45
FEATURE [Part::Cylinder] cylinder084
  Angle = 360
  Height = 45
  Placement = pos=(26.9231,0.1,10) rot=(-1,0,0;1.5708rad)
  Radius = 10
FEATURE [Part::Fuse] union072
  Base = -> cube120
  Tool = -> cylinder084
FEATURE [Part::Cylinder] cylinder085
  Angle = 360
  Height = 3
  Placement = pos=(7.07692,2,10) rot=(1,0,0;1.5708rad)
  Radius = 10.5385
FEATURE [Part::Cylinder] cylinder086
  Angle = 360
  Height = 45.9
  Placement = pos=(29.2308,45.5,10) rot=(1,0,0;1.5708rad)
  Radius = 3.76923
FEATURE [Part::Cylinder] cylinder087
  Angle = 360
  Height = 3
  Placement = pos=(7.07692,46.3,10) rot=(1,0,0;1.5708rad)
  Radius = 10.5385
FEATURE [Part::MultiFuse] union073
  Shapes = -> [cylinder085,cylinder086,cylinder087]
FEATURE [Part::Box] cube121
  Height = 6.15385
  Length = 7.69231
  Placement = pos=(0,-0.5,0) rot=(0,0,1;0rad)
  Width = 45.9
FEATURE [Part::Cylinder] cylinder088
  Angle = 360
  Height = 45.9
  Placement = pos=(7.69231,45.4,8.46154) rot=(1,0,0;1.5708rad)
  Radius = 8.46154
FEATURE [Part::Cut] difference060
  Base = -> cube121
  Tool = -> cylinder088
FEATURE [Part::Box] cube122
  Height = 6.15385
  Length = 7.69231
  Placement = pos=(0,-0.5,9) rot=(0,0,1;0rad)
  Width = 45.9
FEATURE [Part::Cylinder] cylinder089
  Angle = 360
  Height = 45.9
  Placement = pos=(7.69231,45.4,11.5385) rot=(1,0,0;1.5708rad)
  Radius = 8.46154
FEATURE [Part::Cut] difference061
  Base = -> cube122
  Tool = -> cylinder089
FEATURE [Part::MultiFuse] union074
  Shapes = -> [union073,difference060,difference061]
FEATURE [Part::Cut] difference062
  Base = -> union072
  Tool = -> union074
FEATURE [Part::Cylinder] cylinder090
  Angle = 360
  Height = 44.2
  Placement = pos=(6.92308,44.7,10) rot=(1,0,0;1.5708rad)
  Radius = 2.84615
FEATURE [Part::Box] cube123
  Height = 4
  Length = 4
  Placement = pos=(0.538462,-2,6.92308) rot=(0,0,-1;0.349066rad)
  Width = 4
FEATURE [Part::Box] cube124
  Height = 4
  Length = 4
  Placement = pos=(0.538462,18.8,6.92308) rot=(0,0,-1;1.22173rad)
  Width = 4
FEATURE [Part::Fuse] union075
  Base = -> cube123
  Tool = -> cube124
FEATURE [Part::Cut] difference063
  Base = -> cylinder090
  Tool = -> union075
FEATURE [Part::Fuse] union076
  Base = -> difference062
  Tool = -> difference063
FEATURE [Part::Box] cube125
  Height = 17
  Length = 40
  Placement = pos=(-1.53846,3.4,1.5) rot=(0,0,1;0rad)
  Width = 38.4
FEATURE [Part::Box] cube126
  Height = 15.3846
  Length = 12.3077
  Placement = pos=(23.6154,3.4,5.38462) rot=(0,0,1;0rad)
  Width = 38.4
FEATURE [Part::Box] cube127
  Height = 24.6154
  Length = 12.3077
  Placement = pos=(-1.53846,3.4,-2.30769) rot=(0,0,1;0rad)
  Width = 38.4
FEATURE [Part::Box] cube128
  Height = 17
  Length = 9.23077
  Placement = pos=(19.2308,1.6,1.5) rot=(0,0,1;0rad)
  Width = 42
FEATURE [Part::Box] cube129
  Height = 20
  Length = 15.3846
  Placement = pos=(23.6154,1.6,0) rot=(0,0,1;0rad)
  Width = 42
FEATURE [Part::MultiFuse] Group012
  Shapes = -> [cube127,cube128,cube129]
FEATURE [Part::MultiFuse] union077
  Shapes = -> [cube125,cube126,Group012]
FEATURE [Part::Cut] difference064
  Base = -> union076
  Placement = pos=(182.732,85.3694,566) rot=(0.998099,-0.043578,0.043578;4.71049rad)
  Tool = -> union077
FEATURE [Part::Box] cube130
  Height = 20
  Length = 26.9231
  Placement = pos=(0,0.1,0) rot=(0,0,1;0rad)
  Width = 45
FEATURE [Part::Cylinder] cylinder091
  Angle = 360
  Height = 45
  Placement = pos=(26.9231,0.1,10) rot=(-1,0,0;1.5708rad)
  Radius = 10
FEATURE [Part::Fuse] union078
  Base = -> cube130
  Tool = -> cylinder091
FEATURE [Part::Cylinder] cylinder092
  Angle = 360
  Height = 3
  Placement = pos=(7.07692,2,10) rot=(1,0,0;1.5708rad)
  Radius = 10.5385
FEATURE [Part::Cylinder] cylinder093
  Angle = 360
  Height = 45.9
  Placement = pos=(29.2308,45.5,10) rot=(1,0,0;1.5708rad)
  Radius = 3.76923
FEATURE [Part::Cylinder] cylinder094
  Angle = 360
  Height = 3
  Placement = pos=(7.07692,46.3,10) rot=(1,0,0;1.5708rad)
  Radius = 10.5385
FEATURE [Part::MultiFuse] union079
  Shapes = -> [cylinder092,cylinder093,cylinder094]
FEATURE [Part::Box] cube131
  Height = 6.15385
  Length = 7.69231
  Placement = pos=(0,-0.5,0) rot=(0,0,1;0rad)
  Width = 45.9
FEATURE [Part::Cylinder] cylinder095
  Angle = 360
  Height = 45.9
  Placement = pos=(7.69231,45.4,8.46154) rot=(1,0,0;1.5708rad)
  Radius = 8.46154
FEATURE [Part::Cut] difference065
  Base = -> cube131
  Tool = -> cylinder095
FEATURE [Part::Box] cube132
  Height = 6.15385
  Length = 7.69231
  Placement = pos=(0,-0.5,9) rot=(0,0,1;0rad)
  Width = 45.9
FEATURE [Part::Cylinder] cylinder096
  Angle = 360
  Height = 45.9
  Placement = pos=(7.69231,45.4,11.5385) rot=(1,0,0;1.5708rad)
  Radius = 8.46154
FEATURE [Part::Cut] difference066
  Base = -> cube132
  Tool = -> cylinder096
FEATURE [Part::MultiFuse] union080
  Shapes = -> [union079,difference065,difference066]
FEATURE [Part::Cut] difference067
  Base = -> union078
  Tool = -> union080
FEATURE [Part::Cylinder] cylinder097
  Angle = 360
  Height = 44.2
  Placement = pos=(6.92308,44.7,10) rot=(1,0,0;1.5708rad)
  Radius = 2.84615
FEATURE [Part::Box] cube133
  Height = 4
  Length = 4
  Placement = pos=(0.538462,-2,6.92308) rot=(0,0,-1;0.349066rad)
  Width = 4
FEATURE [Part::Box] cube134
  Height = 4
  Length = 4
  Placement = pos=(0.538462,18.8,6.92308) rot=(0,0,-1;1.22173rad)
  Width = 4
FEATURE [Part::Fuse] union081
  Base = -> cube133
  Tool = -> cube134
FEATURE [Part::Cut] difference068
  Base = -> cylinder097
  Tool = -> union081
FEATURE [Part::Fuse] union082
  Base = -> difference067
  Tool = -> difference068
FEATURE [Part::Box] cube135
  Height = 17
  Length = 40
  Placement = pos=(-1.53846,3.4,1.5) rot=(0,0,1;0rad)
  Width = 38.4
FEATURE [Part::Box] cube136
  Height = 15.3846
  Length = 12.3077
  Placement = pos=(23.6154,3.4,5.38462) rot=(0,0,1;0rad)
  Width = 38.4
FEATURE [Part::Box] cube137
  Height = 24.6154
  Length = 12.3077
  Placement = pos=(-1.53846,3.4,-2.30769) rot=(0,0,1;0rad)
  Width = 38.4
FEATURE [Part::Box] cube138
  Height = 17
  Length = 9.23077
  Placement = pos=(19.2308,1.6,1.5) rot=(0,0,1;0rad)
  Width = 42
FEATURE [Part::Box] cube139
  Height = 20
  Length = 15.3846
  Placement = pos=(23.6154,1.6,0) rot=(0,0,1;0rad)
  Width = 42
FEATURE [Part::MultiFuse] Group013
  Shapes = -> [cube137,cube138,cube139]
FEATURE [Part::MultiFuse] union083
  Shapes = -> [cube135,cube136,Group013]
FEATURE [Part::Cut] difference069
  Base = -> union082
  Placement = pos=(206.698,82.2187,566) rot=(0.998099,0.043578,-0.043578;4.71049rad)
  Tool = -> union083
FEATURE [Part::Box] cube140
  Height = 20
  Length = 26.9231
  Placement = pos=(0,0.1,0) rot=(0,0,1;0rad)
  Width = 45
FEATURE [Part::Cylinder] cylinder098
  Angle = 360
  Height = 45
  Placement = pos=(26.9231,0.1,10) rot=(-1,0,0;1.5708rad)
  Radius = 10
FEATURE [Part::Fuse] union084
  Base = -> cube140
  Tool = -> cylinder098
FEATURE [Part::Cylinder] cylinder099
  Angle = 360
  Height = 3
  Placement = pos=(7.07692,2,10) rot=(1,0,0;1.5708rad)
  Radius = 10.5385
FEATURE [Part::Cylinder] cylinder100
  Angle = 360
  Height = 45.9
  Placement = pos=(29.2308,45.5,10) rot=(1,0,0;1.5708rad)
  Radius = 3.76923
FEATURE [Part::Cylinder] cylinder101
  Angle = 360
  Height = 3
  Placement = pos=(7.07692,46.3,10) rot=(1,0,0;1.5708rad)
  Radius = 10.5385
FEATURE [Part::MultiFuse] union085
  Shapes = -> [cylinder099,cylinder100,cylinder101]
FEATURE [Part::Box] cube141
  Height = 6.15385
  Length = 7.69231
  Placement = pos=(0,-0.5,0) rot=(0,0,1;0rad)
  Width = 45.9
FEATURE [Part::Cylinder] cylinder102
  Angle = 360
  Height = 45.9
  Placement = pos=(7.69231,45.4,8.46154) rot=(1,0,0;1.5708rad)
  Radius = 8.46154
FEATURE [Part::Cut] difference070
  Base = -> cube141
  Tool = -> cylinder102
FEATURE [Part::Box] cube142
  Height = 6.15385
  Length = 7.69231
  Placement = pos=(0,-0.5,9) rot=(0,0,1;0rad)
  Width = 45.9
FEATURE [Part::Cylinder] cylinder103
  Angle = 360
  Height = 45.9
  Placement = pos=(7.69231,45.4,11.5385) rot=(1,0,0;1.5708rad)
  Radius = 8.46154
FEATURE [Part::Cut] difference071
  Base = -> cube142
  Tool = -> cylinder103
FEATURE [Part::MultiFuse] union086
  Shapes = -> [union085,difference070,difference071]
FEATURE [Part::Cut] difference072
  Base = -> union084
  Tool = -> union086
FEATURE [Part::Cylinder] cylinder104
  Angle = 360
  Height = 44.2
  Placement = pos=(6.92308,44.7,10) rot=(1,0,0;1.5708rad)
  Radius = 2.84615
FEATURE [Part::Box] cube143
  Height = 4
  Length = 4
  Placement = pos=(0.538462,-2,6.92308) rot=(0,0,-1;0.349066rad)
  Width = 4
FEATURE [Part::Box] cube144
  Height = 4
  Length = 4
  Placement = pos=(0.538462,18.8,6.92308) rot=(0,0,-1;1.22173rad)
  Width = 4
FEATURE [Part::Fuse] union087
  Base = -> cube143
  Tool = -> cube144
FEATURE [Part::Cut] difference073
  Base = -> cylinder104
  Tool = -> union087
FEATURE [Part::Fuse] union088
  Base = -> difference072
  Tool = -> difference073
FEATURE [Part::Box] cube145
  Height = 17
  Length = 40
  Placement = pos=(-1.53846,3.4,1.5) rot=(0,0,1;0rad)
  Width = 38.4
FEATURE [Part::Box] cube146
  Height = 15.3846
  Length = 12.3077
  Placement = pos=(23.6154,3.4,5.38462) rot=(0,0,1;0rad)
  Width = 38.4
FEATURE [Part::Box] cube147
  Height = 24.6154
  Length = 12.3077
  Placement = pos=(-1.53846,3.4,-2.30769) rot=(0,0,1;0rad)
  Width = 38.4
FEATURE [Part::Box] cube148
  Height = 17
  Length = 9.23077
  Placement = pos=(19.2308,1.6,1.5) rot=(0,0,1;0rad)
  Width = 42
FEATURE [Part::Box] cube149
  Height = 20
  Length = 15.3846
  Placement = pos=(23.6154,1.6,0) rot=(0,0,1;0rad)
  Width = 42
FEATURE [Part::MultiFuse] Group014
  Shapes = -> [cube147,cube148,cube149]
FEATURE [Part::MultiFuse] union089
  Shapes = -> [cube145,cube146,Group014]
FEATURE [Part::Cut] difference074
  Base = -> union088
  Placement = pos=(230.847,83.2769,566) rot=(0.983106,0.129428,-0.129428;4.69535rad)
  Tool = -> union089
FEATURE [Part::Box] cube150
  Height = 20
  Length = 26.9231
  Placement = pos=(0,0.1,0) rot=(0,0,1;0rad)
  Width = 45
FEATURE [Part::Cylinder] cylinder105
  Angle = 360
  Height = 45
  Placement = pos=(26.9231,0.1,10) rot=(-1,0,0;1.5708rad)
  Radius = 10
FEATURE [Part::Fuse] union090
  Base = -> cube150
  Tool = -> cylinder105
FEATURE [Part::Cylinder] cylinder106
  Angle = 360
  Height = 3
  Placement = pos=(7.07692,2,10) rot=(1,0,0;1.5708rad)
  Radius = 10.5385
FEATURE [Part::Cylinder] cylinder107
  Angle = 360
  Height = 45.9
  Placement = pos=(29.2308,45.5,10) rot=(1,0,0;1.5708rad)
  Radius = 3.76923
FEATURE [Part::Cylinder] cylinder108
  Angle = 360
  Height = 3
  Placement = pos=(7.07692,46.3,10) rot=(1,0,0;1.5708rad)
  Radius = 10.5385
FEATURE [Part::MultiFuse] union091
  Shapes = -> [cylinder106,cylinder107,cylinder108]
FEATURE [Part::Box] cube151
  Height = 6.15385
  Length = 7.69231
  Placement = pos=(0,-0.5,0) rot=(0,0,1;0rad)
  Width = 45.9
FEATURE [Part::Cylinder] cylinder109
  Angle = 360
  Height = 45.9
  Placement = pos=(7.69231,45.4,8.46154) rot=(1,0,0;1.5708rad)
  Radius = 8.46154
FEATURE [Part::Cut] difference075
  Base = -> cube151
  Tool = -> cylinder109
FEATURE [Part::Box] cube152
  Height = 6.15385
  Length = 7.69231
  Placement = pos=(0,-0.5,9) rot=(0,0,1;0rad)
  Width = 45.9
FEATURE [Part::Cylinder] cylinder110
  Angle = 360
  Height = 45.9
  Placement = pos=(7.69231,45.4,11.5385) rot=(1,0,0;1.5708rad)
  Radius = 8.46154
FEATURE [Part::Cut] difference076
  Base = -> cube152
  Tool = -> cylinder110
FEATURE [Part::MultiFuse] union092
  Shapes = -> [union091,difference075,difference076]
FEATURE [Part::Cut] difference077
  Base = -> union090
  Tool = -> union092
FEATURE [Part::Cylinder] cylinder111
  Angle = 360
  Height = 44.2
  Placement = pos=(6.92308,44.7,10) rot=(1,0,0;1.5708rad)
  Radius = 2.84615
FEATURE [Part::Box] cube153
  Height = 4
  Length = 4
  Placement = pos=(0.538462,-2,6.92308) rot=(0,0,-1;0.349066rad)
  Width = 4
FEATURE [Part::Box] cube154
  Height = 4
  Length = 4
  Placement = pos=(0.538462,18.8,6.92308) rot=(0,0,-1;1.22173rad)
  Width = 4
FEATURE [Part::Fuse] union093
  Base = -> cube153
  Tool = -> cube154
FEATURE [Part::Cut] difference078
  Base = -> cylinder111
  Tool = -> union093
FEATURE [Part::Fuse] union094
  Base = -> difference077
  Tool = -> difference078
FEATURE [Part::Box] cube155
  Height = 17
  Length = 40
  Placement = pos=(-1.53846,3.4,1.5) rot=(0,0,1;0rad)
  Width = 38.4
FEATURE [Part::Box] cube156
  Height = 15.3846
  Length = 12.3077
  Placement = pos=(23.6154,3.4,5.38462) rot=(0,0,1;0rad)
  Width = 38.4
FEATURE [Part::Box] cube157
  Height = 24.6154
  Length = 12.3077
  Placement = pos=(-1.53846,3.4,-2.30769) rot=(0,0,1;0rad)
  Width = 38.4
FEATURE [Part::Box] cube158
  Height = 17
  Length = 9.23077
  Placement = pos=(19.2308,1.6,1.5) rot=(0,0,1;0rad)
  Width = 42
FEATURE [Part::Box] cube159
  Height = 20
  Length = 15.3846
  Placement = pos=(23.6154,1.6,0) rot=(0,0,1;0rad)
  Width = 42
FEATURE [Part::MultiFuse] Group015
  Shapes = -> [cube157,cube158,cube159]
FEATURE [Part::MultiFuse] union095
  Shapes = -> [cube155,cube156,Group015]
FEATURE [Part::Cut] difference079
  Base = -> union094
  Placement = pos=(254.446,88.5131,566) rot=(0.954202,0.211541,-0.211541;4.66553rad)
  Tool = -> union095
FEATURE [Part::Box] cube160
  Height = 20
  Length = 26.9231
  Placement = pos=(0,0.1,0) rot=(0,0,1;0rad)
  Width = 45
FEATURE [Part::Cylinder] cylinder112
  Angle = 360
  Height = 45
  Placement = pos=(26.9231,0.1,10) rot=(-1,0,0;1.5708rad)
  Radius = 10
FEATURE [Part::Fuse] union096
  Base = -> cube160
  Tool = -> cylinder112
FEATURE [Part::Cylinder] cylinder113
  Angle = 360
  Height = 3
  Placement = pos=(7.07692,2,10) rot=(1,0,0;1.5708rad)
  Radius = 10.5385
FEATURE [Part::Cylinder] cylinder114
  Angle = 360
  Height = 45.9
  Placement = pos=(29.2308,45.5,10) rot=(1,0,0;1.5708rad)
  Radius = 3.76923
FEATURE [Part::Cylinder] cylinder115
  Angle = 360
  Height = 3
  Placement = pos=(7.07692,46.3,10) rot=(1,0,0;1.5708rad)
  Radius = 10.5385
FEATURE [Part::MultiFuse] union097
  Shapes = -> [cylinder113,cylinder114,cylinder115]
FEATURE [Part::Box] cube161
  Height = 6.15385
  Length = 7.69231
  Placement = pos=(0,-0.5,0) rot=(0,0,1;0rad)
  Width = 45.9
FEATURE [Part::Cylinder] cylinder116
  Angle = 360
  Height = 45.9
  Placement = pos=(7.69231,45.4,8.46154) rot=(1,0,0;1.5708rad)
  Radius = 8.46154
FEATURE [Part::Cut] difference080
  Base = -> cube161
  Tool = -> cylinder116
FEATURE [Part::Box] cube162
  Height = 6.15385
  Length = 7.69231
  Placement = pos=(0,-0.5,9) rot=(0,0,1;0rad)
  Width = 45.9
FEATURE [Part::Cylinder] cylinder117
  Angle = 360
  Height = 45.9
  Placement = pos=(7.69231,45.4,11.5385) rot=(1,0,0;1.5708rad)
  Radius = 8.46154
FEATURE [Part::Cut] difference081
  Base = -> cube162
  Tool = -> cylinder117
FEATURE [Part::MultiFuse] union098
  Shapes = -> [union097,difference080,difference081]
FEATURE [Part::Cut] difference082
  Base = -> union096
  Tool = -> union098
FEATURE [Part::Cylinder] cylinder118
  Angle = 360
  Height = 44.2
  Placement = pos=(6.92308,44.7,10) rot=(1,0,0;1.5708rad)
  Radius = 2.84615
FEATURE [Part::Box] cube163
  Height = 4
  Length = 4
  Placement = pos=(0.538462,-2,6.92308) rot=(0,0,-1;0.349066rad)
  Width = 4
FEATURE [Part::Box] cube164
  Height = 4
  Length = 4
  Placement = pos=(0.538462,18.8,6.92308) rot=(0,0,-1;1.22173rad)
  Width = 4
FEATURE [Part::Fuse] union099
  Base = -> cube163
  Tool = -> cube164
FEATURE [Part::Cut] difference083
  Base = -> cylinder118
  Tool = -> union099
FEATURE [Part::Fuse] union100
  Base = -> difference082
  Tool = -> difference083
FEATURE [Part::Box] cube165
  Height = 17
  Length = 40
  Placement = pos=(-1.53846,3.4,1.5) rot=(0,0,1;0rad)
  Width = 38.4
FEATURE [Part::Box] cube166
  Height = 15.3846
  Length = 12.3077
  Placement = pos=(23.6154,3.4,5.38462) rot=(0,0,1;0rad)
  Width = 38.4
FEATURE [Part::Box] cube167
  Height = 24.6154
  Length = 12.3077
  Placement = pos=(-1.53846,3.4,-2.30769) rot=(0,0,1;0rad)
  Width = 38.4
FEATURE [Part::Box] cube168
  Height = 17
  Length = 9.23077
  Placement = pos=(19.2308,1.6,1.5) rot=(0,0,1;0rad)
  Width = 42
FEATURE [Part::Box] cube169
  Height = 20
  Length = 15.3846
  Placement = pos=(23.6154,1.6,0) rot=(0,0,1;0rad)
  Width = 42
FEATURE [Part::MultiFuse] Group016
  Shapes = -> [cube167,cube168,cube169]
FEATURE [Part::MultiFuse] union101
  Shapes = -> [cube165,cube166,Group016]
FEATURE [Part::Cut] difference084
  Base = -> union100
  Placement = pos=(276.14,97.7808,566) rot=(0.926703,0.265728,-0.265728;4.63634rad)
  Tool = -> union101
FEATURE [Part::Box] cube170
  Height = 20
  Length = 26.9231
  Placement = pos=(0,0.1,0) rot=(0,0,1;0rad)
  Width = 45
FEATURE [Part::Cylinder] cylinder119
  Angle = 360
  Height = 45
  Placement = pos=(26.9231,0.1,10) rot=(-1,0,0;1.5708rad)
  Radius = 10
FEATURE [Part::Fuse] union102
  Base = -> cube170
  Tool = -> cylinder119
FEATURE [Part::Cylinder] cylinder120
  Angle = 360
  Height = 3
  Placement = pos=(7.07692,2,10) rot=(1,0,0;1.5708rad)
  Radius = 10.5385
FEATURE [Part::Cylinder] cylinder121
  Angle = 360
  Height = 45.9
  Placement = pos=(29.2308,45.5,10) rot=(1,0,0;1.5708rad)
  Radius = 3.76923
FEATURE [Part::Cylinder] cylinder122
  Angle = 360
  Height = 3
  Placement = pos=(7.07692,46.3,10) rot=(1,0,0;1.5708rad)
  Radius = 10.5385
FEATURE [Part::MultiFuse] union103
  Shapes = -> [cylinder120,cylinder121,cylinder122]
FEATURE [Part::Box] cube171
  Height = 6.15385
  Length = 7.69231
  Placement = pos=(0,-0.5,0) rot=(0,0,1;0rad)
  Width = 45.9
FEATURE [Part::Cylinder] cylinder123
  Angle = 360
  Height = 45.9
  Placement = pos=(7.69231,45.4,8.46154) rot=(1,0,0;1.5708rad)
  Radius = 8.46154
FEATURE [Part::Cut] difference085
  Base = -> cube171
  Tool = -> cylinder123
FEATURE [Part::Box] cube172
  Height = 6.15385
  Length = 7.69231
  Placement = pos=(0,-0.5,9) rot=(0,0,1;0rad)
  Width = 45.9
FEATURE [Part::Cylinder] cylinder124
  Angle = 360
  Height = 45.9
  Placement = pos=(7.69231,45.4,11.5385) rot=(1,0,0;1.5708rad)
  Radius = 8.46154
FEATURE [Part::Cut] difference086
  Base = -> cube172
  Tool = -> cylinder124
FEATURE [Part::MultiFuse] union104
  Shapes = -> [union103,difference085,difference086]
FEATURE [Part::Cut] difference087
  Base = -> union102
  Tool = -> union104
FEATURE [Part::Cylinder] cylinder125
  Angle = 360
  Height = 44.2
  Placement = pos=(6.92308,44.7,10) rot=(1,0,0;1.5708rad)
  Radius = 2.84615
FEATURE [Part::Box] cube173
  Height = 4
  Length = 4
  Placement = pos=(0.538462,-2,6.92308) rot=(0,0,-1;0.349066rad)
  Width = 4
FEATURE [Part::Box] cube174
  Height = 4
  Length = 4
  Placement = pos=(0.538462,18.8,6.92308) rot=(0,0,-1;1.22173rad)
  Width = 4
FEATURE [Part::Fuse] union105
  Base = -> cube173
  Tool = -> cube174
FEATURE [Part::Cut] difference088
  Base = -> cylinder125
  Tool = -> union105
FEATURE [Part::Fuse] union106
  Base = -> difference087
  Tool = -> difference088
FEATURE [Part::Box] cube175
  Height = 17
  Length = 40
  Placement = pos=(-1.53846,3.4,1.5) rot=(0,0,1;0rad)
  Width = 38.4
FEATURE [Part::Box] cube176
  Height = 15.3846
  Length = 12.3077
  Placement = pos=(23.6154,3.4,5.38462) rot=(0,0,1;0rad)
  Width = 38.4
FEATURE [Part::Box] cube177
  Height = 24.6154
  Length = 12.3077
  Placement = pos=(-1.53846,3.4,-2.30769) rot=(0,0,1;0rad)
  Width = 38.4
FEATURE [Part::Box] cube178
  Height = 17
  Length = 9.23077
  Placement = pos=(19.2308,1.6,1.5) rot=(0,0,1;0rad)
  Width = 42
FEATURE [Part::Box] cube179
  Height = 20
  Length = 15.3846
  Placement = pos=(23.6154,1.6,0) rot=(0,0,1;0rad)
  Width = 42
FEATURE [Part::MultiFuse] Group017
  Shapes = -> [cube177,cube178,cube179]
FEATURE [Part::MultiFuse] union107
  Shapes = -> [cube175,cube176,Group017]
FEATURE [Part::Cut] difference089
  Base = -> union106
  Placement = pos=(296.331,109.609,566) rot=(0.89907,0.309574,-0.309574;4.60619rad)
  Tool = -> union107
FEATURE [Part::Box] cube180
  Height = 20
  Length = 26.9231
  Placement = pos=(0,0.1,0) rot=(0,0,1;0rad)
  Width = 45
FEATURE [Part::Cylinder] cylinder126
  Angle = 360
  Height = 45
  Placement = pos=(26.9231,0.1,10) rot=(-1,0,0;1.5708rad)
  Radius = 10
FEATURE [Part::Fuse] union108
  Base = -> cube180
  Tool = -> cylinder126
FEATURE [Part::Cylinder] cylinder127
  Angle = 360
  Height = 3
  Placement = pos=(7.07692,2,10) rot=(1,0,0;1.5708rad)
  Radius = 10.5385
FEATURE [Part::Cylinder] cylinder128
  Angle = 360
  Height = 45.9
  Placement = pos=(29.2308,45.5,10) rot=(1,0,0;1.5708rad)
  Radius = 3.76923
FEATURE [Part::Cylinder] cylinder129
  Angle = 360
  Height = 3
  Placement = pos=(7.07692,46.3,10) rot=(1,0,0;1.5708rad)
  Radius = 10.5385
FEATURE [Part::MultiFuse] union109
  Shapes = -> [cylinder127,cylinder128,cylinder129]
FEATURE [Part::Box] cube181
  Height = 6.15385
  Length = 7.69231
  Placement = pos=(0,-0.5,0) rot=(0,0,1;0rad)
  Width = 45.9
FEATURE [Part::Cylinder] cylinder130
  Angle = 360
  Height = 45.9
  Placement = pos=(7.69231,45.4,8.46154) rot=(1,0,0;1.5708rad)
  Radius = 8.46154
FEATURE [Part::Cut] difference090
  Base = -> cube181
  Tool = -> cylinder130
FEATURE [Part::Box] cube182
  Height = 6.15385
  Length = 7.69231
  Placement = pos=(0,-0.5,9) rot=(0,0,1;0rad)
  Width = 45.9
FEATURE [Part::Cylinder] cylinder131
  Angle = 360
  Height = 45.9
  Placement = pos=(7.69231,45.4,11.5385) rot=(1,0,0;1.5708rad)
  Radius = 8.46154
FEATURE [Part::Cut] difference091
  Base = -> cube182
  Tool = -> cylinder131
FEATURE [Part::MultiFuse] union110
  Shapes = -> [union109,difference090,difference091]
FEATURE [Part::Cut] difference092
  Base = -> union108
  Tool = -> union110
FEATURE [Part::Cylinder] cylinder132
  Angle = 360
  Height = 44.2
  Placement = pos=(6.92308,44.7,10) rot=(1,0,0;1.5708rad)
  Radius = 2.84615
FEATURE [Part::Box] cube183
  Height = 4
  Length = 4
  Placement = pos=(0.538462,-2,6.92308) rot=(0,0,-1;0.349066rad)
  Width = 4
FEATURE [Part::Box] cube184
  Height = 4
  Length = 4
  Placement = pos=(0.538462,18.8,6.92308) rot=(0,0,-1;1.22173rad)
  Width = 4
FEATURE [Part::Fuse] union111
  Base = -> cube183
  Tool = -> cube184
FEATURE [Part::Cut] difference093
  Base = -> cylinder132
  Tool = -> union111
FEATURE [Part::Fuse] union112
  Base = -> difference092
  Tool = -> difference093
FEATURE [Part::Box] cube185
  Height = 17
  Length = 40
  Placement = pos=(-1.53846,3.4,1.5) rot=(0,0,1;0rad)
  Width = 38.4
FEATURE [Part::Box] cube186
  Height = 15.3846
  Length = 12.3077
  Placement = pos=(23.6154,3.4,5.38462) rot=(0,0,1;0rad)
  Width = 38.4
FEATURE [Part::Box] cube187
  Height = 24.6154
  Length = 12.3077
  Placement = pos=(-1.53846,3.4,-2.30769) rot=(0,0,1;0rad)
  Width = 38.4
FEATURE [Part::Box] cube188
  Height = 17
  Length = 9.23077
  Placement = pos=(19.2308,1.6,1.5) rot=(0,0,1;0rad)
  Width = 42
FEATURE [Part::Box] cube189
  Height = 20
  Length = 15.3846
  Placement = pos=(23.6154,1.6,0) rot=(0,0,1;0rad)
  Width = 42
FEATURE [Part::MultiFuse] Group018
  Shapes = -> [cube187,cube188,cube189]
FEATURE [Part::MultiFuse] union113
  Shapes = -> [cube185,cube186,Group018]
FEATURE [Part::Cut] difference094
  Base = -> union112
  Placement = pos=(314.965,123.45,566) rot=(0.873594,0.344118,-0.344118;4.57766rad)
  Tool = -> union113
FEATURE [Part::Box] cube190
  Height = 20
  Length = 26.9231
  Placement = pos=(0,0.1,0) rot=(0,0,1;0rad)
  Width = 45
FEATURE [Part::Cylinder] cylinder133
  Angle = 360
  Height = 45
  Placement = pos=(26.9231,0.1,10) rot=(-1,0,0;1.5708rad)
  Radius = 10
FEATURE [Part::Fuse] union114
  Base = -> cube190
  Tool = -> cylinder133
FEATURE [Part::Cylinder] cylinder134
  Angle = 360
  Height = 3
  Placement = pos=(7.07692,2,10) rot=(1,0,0;1.5708rad)
  Radius = 10.5385
FEATURE [Part::Cylinder] cylinder135
  Angle = 360
  Height = 45.9
  Placement = pos=(29.2308,45.5,10) rot=(1,0,0;1.5708rad)
  Radius = 3.76923
FEATURE [Part::Cylinder] cylinder136
  Angle = 360
  Height = 3
  Placement = pos=(7.07692,46.3,10) rot=(1,0,0;1.5708rad)
  Radius = 10.5385
FEATURE [Part::MultiFuse] union115
  Shapes = -> [cylinder134,cylinder135,cylinder136]
FEATURE [Part::Box] cube191
  Height = 6.15385
  Length = 7.69231
  Placement = pos=(0,-0.5,0) rot=(0,0,1;0rad)
  Width = 45.9
FEATURE [Part::Cylinder] cylinder137
  Angle = 360
  Height = 45.9
  Placement = pos=(7.69231,45.4,8.46154) rot=(1,0,0;1.5708rad)
  Radius = 8.46154
FEATURE [Part::Cut] difference095
  Base = -> cube191
  Tool = -> cylinder137
FEATURE [Part::Box] cube192
  Height = 6.15385
  Length = 7.69231
  Placement = pos=(0,-0.5,9) rot=(0,0,1;0rad)
  Width = 45.9
FEATURE [Part::Cylinder] cylinder138
  Angle = 360
  Height = 45.9
  Placement = pos=(7.69231,45.4,11.5385) rot=(1,0,0;1.5708rad)
  Radius = 8.46154
FEATURE [Part::Cut] difference096
  Base = -> cube192
  Tool = -> cylinder138
FEATURE [Part::MultiFuse] union116
  Shapes = -> [union115,difference095,difference096]
FEATURE [Part::Cut] difference097
  Base = -> union114
  Tool = -> union116
FEATURE [Part::Cylinder] cylinder139
  Angle = 360
  Height = 44.2
  Placement = pos=(6.92308,44.7,10) rot=(1,0,0;1.5708rad)
  Radius = 2.84615
FEATURE [Part::Box] cube193
  Height = 4
  Length = 4
  Placement = pos=(0.538462,-2,6.92308) rot=(0,0,-1;0.349066rad)
  Width = 4
FEATURE [Part::Box] cube194
  Height = 4
  Length = 4
  Placement = pos=(0.538462,18.8,6.92308) rot=(0,0,-1;1.22173rad)
  Width = 4
FEATURE [Part::Fuse] union117
  Base = -> cube193
  Tool = -> cube194
FEATURE [Part::Cut] difference098
  Base = -> cylinder139
  Tool = -> union117
FEATURE [Part::Fuse] union118
  Base = -> difference097
  Tool = -> difference098
FEATURE [Part::Box] cube195
  Height = 17
  Length = 40
  Placement = pos=(-1.53846,3.4,1.5) rot=(0,0,1;0rad)
  Width = 38.4
FEATURE [Part::Box] cube196
  Height = 15.3846
  Length = 12.3077
  Placement = pos=(23.6154,3.4,5.38462) rot=(0,0,1;0rad)
  Width = 38.4
FEATURE [Part::Box] cube197
  Height = 24.6154
  Length = 12.3077
  Placement = pos=(-1.53846,3.4,-2.30769) rot=(0,0,1;0rad)
  Width = 38.4
FEATURE [Part::Box] cube198
  Height = 17
  Length = 9.23077
  Placement = pos=(19.2308,1.6,1.5) rot=(0,0,1;0rad)
  Width = 42
FEATURE [Part::Box] cube199
  Height = 20
  Length = 15.3846
  Placement = pos=(23.6154,1.6,0) rot=(0,0,1;0rad)
  Width = 42
FEATURE [Part::MultiFuse] Group019
  Shapes = -> [cube197,cube198,cube199]
FEATURE [Part::MultiFuse] union119
  Shapes = -> [cube195,cube196,Group019]
FEATURE [Part::Cut] difference099
  Base = -> union118
  Placement = pos=(332.322,138.863,566) rot=(-0.846226,-0.376764,0.376764;1.737rad)
  Tool = -> union119
FEATURE [Part::Box] cube200
  Height = 20
  Length = 26.9231
  Placement = pos=(0,0.1,0) rot=(0,0,1;0rad)
  Width = 45
FEATURE [Part::Cylinder] cylinder140
  Angle = 360
  Height = 45
  Placement = pos=(26.9231,0.1,10) rot=(-1,0,0;1.5708rad)
  Radius = 10
FEATURE [Part::Fuse] union120
  Base = -> cube200
  Tool = -> cylinder140
FEATURE [Part::Cylinder] cylinder141
  Angle = 360
  Height = 3
  Placement = pos=(7.07692,2,10) rot=(1,0,0;1.5708rad)
  Radius = 10.5385
FEATURE [Part::Cylinder] cylinder142
  Angle = 360
  Height = 45.9
  Placement = pos=(29.2308,45.5,10) rot=(1,0,0;1.5708rad)
  Radius = 3.76923
FEATURE [Part::Cylinder] cylinder143
  Angle = 360
  Height = 3
  Placement = pos=(7.07692,46.3,10) rot=(1,0,0;1.5708rad)
  Radius = 10.5385
FEATURE [Part::MultiFuse] union121
  Shapes = -> [cylinder141,cylinder142,cylinder143]
FEATURE [Part::Box] cube201
  Height = 6.15385
  Length = 7.69231
  Placement = pos=(0,-0.5,0) rot=(0,0,1;0rad)
  Width = 45.9
FEATURE [Part::Cylinder] cylinder144
  Angle = 360
  Height = 45.9
  Placement = pos=(7.69231,45.4,8.46154) rot=(1,0,0;1.5708rad)
  Radius = 8.46154
FEATURE [Part::Cut] difference100
  Base = -> cube201
  Tool = -> cylinder144
FEATURE [Part::Box] cube202
  Height = 6.15385
  Length = 7.69231
  Placement = pos=(0,-0.5,9) rot=(0,0,1;0rad)
  Width = 45.9
FEATURE [Part::Cylinder] cylinder145
  Angle = 360
  Height = 45.9
  Placement = pos=(7.69231,45.4,11.5385) rot=(1,0,0;1.5708rad)
  Radius = 8.46154
FEATURE [Part::Cut] difference101
  Base = -> cube202
  Tool = -> cylinder145
FEATURE [Part::MultiFuse] union122
  Shapes = -> [union121,difference100,difference101]
FEATURE [Part::Cut] difference102
  Base = -> union120
  Tool = -> union122
FEATURE [Part::Cylinder] cylinder146
  Angle = 360
  Height = 44.2
  Placement = pos=(6.92308,44.7,10) rot=(1,0,0;1.5708rad)
  Radius = 2.84615
FEATURE [Part::Box] cube203
  Height = 4
  Length = 4
  Placement = pos=(0.538462,-2,6.92308) rot=(0,0,-1;0.349066rad)
  Width = 4
FEATURE [Part::Box] cube204
  Height = 4
  Length = 4
  Placement = pos=(0.538462,18.8,6.92308) rot=(0,0,-1;1.22173rad)
  Width = 4
FEATURE [Part::Fuse] union123
  Base = -> cube203
  Tool = -> cube204
FEATURE [Part::Cut] difference103
  Base = -> cylinder146
  Tool = -> union123
FEATURE [Part::Fuse] union124
  Base = -> difference102
  Tool = -> difference103
FEATURE [Part::Box] cube205
  Height = 17
  Length = 40
  Placement = pos=(-1.53846,3.4,1.5) rot=(0,0,1;0rad)
  Width = 38.4
FEATURE [Part::Box] cube206
  Height = 15.3846
  Length = 12.3077
  Placement = pos=(23.6154,3.4,5.38462) rot=(0,0,1;0rad)
  Width = 38.4
FEATURE [Part::Box] cube207
  Height = 24.6154
  Length = 12.3077
  Placement = pos=(-1.53846,3.4,-2.30769) rot=(0,0,1;0rad)
  Width = 38.4
FEATURE [Part::Box] cube208
  Height = 17
  Length = 9.23077
  Placement = pos=(19.2308,1.6,1.5) rot=(0,0,1;0rad)
  Width = 42
FEATURE [Part::Box] cube209
  Height = 20
  Length = 15.3846
  Placement = pos=(23.6154,1.6,0) rot=(0,0,1;0rad)
  Width = 42
FEATURE [Part::MultiFuse] Group020
  Shapes = -> [cube207,cube208,cube209]
FEATURE [Part::MultiFuse] union125
  Shapes = -> [cube205,cube206,Group020]
FEATURE [Part::Cut] difference104
  Base = -> union124
  Placement = pos=(348.27,155.729,566) rot=(0.817268,0.407475,-0.407475;4.51196rad)
  Tool = -> union125
FEATURE [Part::Box] cube210
  Height = 20
  Length = 26.9231
  Placement = pos=(0,0.1,0) rot=(0,0,1;0rad)
  Width = 45
FEATURE [Part::Cylinder] cylinder147
  Angle = 360
  Height = 45
  Placement = pos=(26.9231,0.1,10) rot=(-1,0,0;1.5708rad)
  Radius = 10
FEATURE [Part::Fuse] union126
  Base = -> cube210
  Tool = -> cylinder147
FEATURE [Part::Cylinder] cylinder148
  Angle = 360
  Height = 3
  Placement = pos=(7.07692,2,10) rot=(1,0,0;1.5708rad)
  Radius = 10.5385
FEATURE [Part::Cylinder] cylinder149
  Angle = 360
  Height = 45.9
  Placement = pos=(29.2308,45.5,10) rot=(1,0,0;1.5708rad)
  Radius = 3.76923
FEATURE [Part::Cylinder] cylinder150
  Angle = 360
  Height = 3
  Placement = pos=(7.07692,46.3,10) rot=(1,0,0;1.5708rad)
  Radius = 10.5385
FEATURE [Part::MultiFuse] union127
  Shapes = -> [cylinder148,cylinder149,cylinder150]
FEATURE [Part::Box] cube211
  Height = 6.15385
  Length = 7.69231
  Placement = pos=(0,-0.5,0) rot=(0,0,1;0rad)
  Width = 45.9
FEATURE [Part::Cylinder] cylinder151
  Angle = 360
  Height = 45.9
  Placement = pos=(7.69231,45.4,8.46154) rot=(1,0,0;1.5708rad)
  Radius = 8.46154
FEATURE [Part::Cut] difference105
  Base = -> cube211
  Tool = -> cylinder151
FEATURE [Part::Box] cube212
  Height = 6.15385
  Length = 7.69231
  Placement = pos=(0,-0.5,9) rot=(0,0,1;0rad)
  Width = 45.9
FEATURE [Part::Cylinder] cylinder152
  Angle = 360
  Height = 45.9
  Placement = pos=(7.69231,45.4,11.5385) rot=(1,0,0;1.5708rad)
  Radius = 8.46154
FEATURE [Part::Cut] difference106
  Base = -> cube212
  Tool = -> cylinder152
FEATURE [Part::MultiFuse] union128
  Shapes = -> [union127,difference105,difference106]
FEATURE [Part::Cut] difference107
  Base = -> union126
  Tool = -> union128
FEATURE [Part::Cylinder] cylinder153
  Angle = 360
  Height = 44.2
  Placement = pos=(6.92308,44.7,10) rot=(1,0,0;1.5708rad)
  Radius = 2.84615
FEATURE [Part::Box] cube213
  Height = 4
  Length = 4
  Placement = pos=(0.538462,-2,6.92308) rot=(0,0,-1;0.349066rad)
  Width = 4
FEATURE [Part::Box] cube214
  Height = 4
  Length = 4
  Placement = pos=(0.538462,18.8,6.92308) rot=(0,0,-1;1.22173rad)
  Width = 4
FEATURE [Part::Fuse] union129
  Base = -> cube213
  Tool = -> cube214
FEATURE [Part::Cut] difference108
  Base = -> cylinder153
  Tool = -> union129
FEATURE [Part::Fuse] union130
  Base = -> difference107
  Tool = -> difference108
FEATURE [Part::Box] cube215
  Height = 17
  Length = 40
  Placement = pos=(-1.53846,3.4,1.5) rot=(0,0,1;0rad)
  Width = 38.4
FEATURE [Part::Box] cube216
  Height = 15.3846
  Length = 12.3077
  Placement = pos=(23.6154,3.4,5.38462) rot=(0,0,1;0rad)
  Width = 38.4
FEATURE [Part::Box] cube217
  Height = 24.6154
  Length = 12.3077
  Placement = pos=(-1.53846,3.4,-2.30769) rot=(0,0,1;0rad)
  Width = 38.4
FEATURE [Part::Box] cube218
  Height = 17
  Length = 9.23077
  Placement = pos=(19.2308,1.6,1.5) rot=(0,0,1;0rad)
  Width = 42
FEATURE [Part::Box] cube219
  Height = 20
  Length = 15.3846
  Placement = pos=(23.6154,1.6,0) rot=(0,0,1;0rad)
  Width = 42
FEATURE [Part::MultiFuse] Group021
  Shapes = -> [cube217,cube218,cube219]
FEATURE [Part::MultiFuse] union131
  Shapes = -> [cube215,cube216,Group021]
FEATURE [Part::Cut] difference109
  Base = -> union130
  Placement = pos=(362.687,173.922,566) rot=(0.787007,0.436245,-0.436245;4.47513rad)
  Tool = -> union131
FEATURE [Part::Box] cube220
  Height = 20
  Length = 26.9231
  Placement = pos=(0,0.1,0) rot=(0,0,1;0rad)
  Width = 45
FEATURE [Part::Cylinder] cylinder154
  Angle = 360
  Height = 45
  Placement = pos=(26.9231,0.1,10) rot=(-1,0,0;1.5708rad)
  Radius = 10
FEATURE [Part::Fuse] union132
  Base = -> cube220
  Tool = -> cylinder154
FEATURE [Part::Cylinder] cylinder155
  Angle = 360
  Height = 3
  Placement = pos=(7.07692,2,10) rot=(1,0,0;1.5708rad)
  Radius = 10.5385
FEATURE [Part::Cylinder] cylinder156
  Angle = 360
  Height = 45.9
  Placement = pos=(29.2308,45.5,10) rot=(1,0,0;1.5708rad)
  Radius = 3.76923
FEATURE [Part::Cylinder] cylinder157
  Angle = 360
  Height = 3
  Placement = pos=(7.07692,46.3,10) rot=(1,0,0;1.5708rad)
  Radius = 10.5385
FEATURE [Part::MultiFuse] union133
  Shapes = -> [cylinder155,cylinder156,cylinder157]
FEATURE [Part::Box] cube221
  Height = 6.15385
  Length = 7.69231
  Placement = pos=(0,-0.5,0) rot=(0,0,1;0rad)
  Width = 45.9
FEATURE [Part::Cylinder] cylinder158
  Angle = 360
  Height = 45.9
  Placement = pos=(7.69231,45.4,8.46154) rot=(1,0,0;1.5708rad)
  Radius = 8.46154
FEATURE [Part::Cut] difference110
  Base = -> cube221
  Tool = -> cylinder158
FEATURE [Part::Box] cube222
  Height = 6.15385
  Length = 7.69231
  Placement = pos=(0,-0.5,9) rot=(0,0,1;0rad)
  Width = 45.9
FEATURE [Part::Cylinder] cylinder159
  Angle = 360
  Height = 45.9
  Placement = pos=(7.69231,45.4,11.5385) rot=(1,0,0;1.5708rad)
  Radius = 8.46154
FEATURE [Part::Cut] difference111
  Base = -> cube222
  Tool = -> cylinder159
FEATURE [Part::MultiFuse] union134
  Shapes = -> [union133,difference110,difference111]
FEATURE [Part::Cut] difference112
  Base = -> union132
  Tool = -> union134
FEATURE [Part::Cylinder] cylinder160
  Angle = 360
  Height = 44.2
  Placement = pos=(6.92308,44.7,10) rot=(1,0,0;1.5708rad)
  Radius = 2.84615
FEATURE [Part::Box] cube223
  Height = 4
  Length = 4
  Placement = pos=(0.538462,-2,6.92308) rot=(0,0,-1;0.349066rad)
  Width = 4
FEATURE [Part::Box] cube224
  Height = 4
  Length = 4
  Placement = pos=(0.538462,18.8,6.92308) rot=(0,0,-1;1.22173rad)
  Width = 4
FEATURE [Part::Fuse] union135
  Base = -> cube223
  Tool = -> cube224
FEATURE [Part::Cut] difference113
  Base = -> cylinder160
  Tool = -> union135
FEATURE [Part::Fuse] union136
  Base = -> difference112
  Tool = -> difference113
FEATURE [Part::Box] cube225
  Height = 17
  Length = 40
  Placement = pos=(-1.53846,3.4,1.5) rot=(0,0,1;0rad)
  Width = 38.4
FEATURE [Part::Box] cube226
  Height = 15.3846
  Length = 12.3077
  Placement = pos=(23.6154,3.4,5.38462) rot=(0,0,1;0rad)
  Width = 38.4
FEATURE [Part::Box] cube227
  Height = 24.6154
  Length = 12.3077
  Placement = pos=(-1.53846,3.4,-2.30769) rot=(0,0,1;0rad)
  Width = 38.4
FEATURE [Part::Box] cube228
  Height = 17
  Length = 9.23077
  Placement = pos=(19.2308,1.6,1.5) rot=(0,0,1;0rad)
  Width = 42
FEATURE [Part::Box] cube229
  Height = 20
  Length = 15.3846
  Placement = pos=(23.6154,1.6,0) rot=(0,0,1;0rad)
  Width = 42
FEATURE [Part::MultiFuse] Group022
  Shapes = -> [cube227,cube228,cube229]
FEATURE [Part::MultiFuse] union137
  Shapes = -> [cube225,cube226,Group022]
FEATURE [Part::Cut] difference114
  Base = -> union136
  Placement = pos=(375.463,193.302,566) rot=(-0.755702,-0.463095,0.463095;1.84731rad)
  Tool = -> union137
FEATURE [Part::Box] cube230
  Height = 20
  Length = 26.9231
  Placement = pos=(0,0.1,0) rot=(0,0,1;0rad)
  Width = 45
FEATURE [Part::Cylinder] cylinder161
  Angle = 360
  Height = 45
  Placement = pos=(26.9231,0.1,10) rot=(-1,0,0;1.5708rad)
  Radius = 10
FEATURE [Part::Fuse] union138
  Base = -> cube230
  Tool = -> cylinder161
FEATURE [Part::Cylinder] cylinder162
  Angle = 360
  Height = 3
  Placement = pos=(7.07692,2,10) rot=(1,0,0;1.5708rad)
  Radius = 10.5385
FEATURE [Part::Cylinder] cylinder163
  Angle = 360
  Height = 45.9
  Placement = pos=(29.2308,45.5,10) rot=(1,0,0;1.5708rad)
  Radius = 3.76923
FEATURE [Part::Cylinder] cylinder164
  Angle = 360
  Height = 3
  Placement = pos=(7.07692,46.3,10) rot=(1,0,0;1.5708rad)
  Radius = 10.5385
FEATURE [Part::MultiFuse] union139
  Shapes = -> [cylinder162,cylinder163,cylinder164]
FEATURE [Part::Box] cube231
  Height = 6.15385
  Length = 7.69231
  Placement = pos=(0,-0.5,0) rot=(0,0,1;0rad)
  Width = 45.9
FEATURE [Part::Cylinder] cylinder165
  Angle = 360
  Height = 45.9
  Placement = pos=(7.69231,45.4,8.46154) rot=(1,0,0;1.5708rad)
  Radius = 8.46154
FEATURE [Part::Cut] difference115
  Base = -> cube231
  Tool = -> cylinder165
FEATURE [Part::Box] cube232
  Height = 6.15385
  Length = 7.69231
  Placement = pos=(0,-0.5,9) rot=(0,0,1;0rad)
  Width = 45.9
FEATURE [Part::Cylinder] cylinder166
  Angle = 360
  Height = 45.9
  Placement = pos=(7.69231,45.4,11.5385) rot=(1,0,0;1.5708rad)
  Radius = 8.46154
FEATURE [Part::Cut] difference116
  Base = -> cube232
  Tool = -> cylinder166
FEATURE [Part::MultiFuse] union140
  Shapes = -> [union139,difference115,difference116]
FEATURE [Part::Cut] difference117
  Base = -> union138
  Tool = -> union140
FEATURE [Part::Cylinder] cylinder167
  Angle = 360
  Height = 44.2
  Placement = pos=(6.92308,44.7,10) rot=(1,0,0;1.5708rad)
  Radius = 2.84615
FEATURE [Part::Box] cube233
  Height = 4
  Length = 4
  Placement = pos=(0.538462,-2,6.92308) rot=(0,0,-1;0.349066rad)
  Width = 4
FEATURE [Part::Box] cube234
  Height = 4
  Length = 4
  Placement = pos=(0.538462,18.8,6.92308) rot=(0,0,-1;1.22173rad)
  Width = 4
FEATURE [Part::Fuse] union141
  Base = -> cube233
  Tool = -> cube234
FEATURE [Part::Cut] difference118
  Base = -> cylinder167
  Tool = -> union141
FEATURE [Part::Fuse] union142
  Base = -> difference117
  Tool = -> difference118
FEATURE [Part::Box] cube235
  Height = 17
  Length = 40
  Placement = pos=(-1.53846,3.4,1.5) rot=(0,0,1;0rad)
  Width = 38.4
FEATURE [Part::Box] cube236
  Height = 15.3846
  Length = 12.3077
  Placement = pos=(23.6154,3.4,5.38462) rot=(0,0,1;0rad)
  Width = 38.4
FEATURE [Part::Box] cube237
  Height = 24.6154
  Length = 12.3077
  Placement = pos=(-1.53846,3.4,-2.30769) rot=(0,0,1;0rad)
  Width = 38.4
FEATURE [Part::Box] cube238
  Height = 17
  Length = 9.23077
  Placement = pos=(19.2308,1.6,1.5) rot=(0,0,1;0rad)
  Width = 42
FEATURE [Part::Box] cube239
  Height = 20
  Length = 15.3846
  Placement = pos=(23.6154,1.6,0) rot=(0,0,1;0rad)
  Width = 42
FEATURE [Part::MultiFuse] Group023
  Shapes = -> [cube237,cube238,cube239]
FEATURE [Part::MultiFuse] union143
  Shapes = -> [cube235,cube236,Group023]
FEATURE [Part::Cut] difference119
  Base = -> union142
  Placement = pos=(386.502,213.722,566) rot=(-0.723589,-0.488067,0.488067;1.88883rad)
  Tool = -> union143
FEATURE [Part::Box] cube240
  Height = 20
  Length = 26.9231
  Placement = pos=(0,0.1,0) rot=(0,0,1;0rad)
  Width = 45
FEATURE [Part::Cylinder] cylinder168
  Angle = 360
  Height = 45
  Placement = pos=(26.9231,0.1,10) rot=(-1,0,0;1.5708rad)
  Radius = 10
FEATURE [Part::Fuse] union144
  Base = -> cube240
  Tool = -> cylinder168
FEATURE [Part::Cylinder] cylinder169
  Angle = 360
  Height = 3
  Placement = pos=(7.07692,2,10) rot=(1,0,0;1.5708rad)
  Radius = 10.5385
FEATURE [Part::Cylinder] cylinder170
  Angle = 360
  Height = 45.9
  Placement = pos=(29.2308,45.5,10) rot=(1,0,0;1.5708rad)
  Radius = 3.76923
FEATURE [Part::Cylinder] cylinder171
  Angle = 360
  Height = 3
  Placement = pos=(7.07692,46.3,10) rot=(1,0,0;1.5708rad)
  Radius = 10.5385
FEATURE [Part::MultiFuse] union145
  Shapes = -> [cylinder169,cylinder170,cylinder171]
FEATURE [Part::Box] cube241
  Height = 6.15385
  Length = 7.69231
  Placement = pos=(0,-0.5,0) rot=(0,0,1;0rad)
  Width = 45.9
FEATURE [Part::Cylinder] cylinder172
  Angle = 360
  Height = 45.9
  Placement = pos=(7.69231,45.4,8.46154) rot=(1,0,0;1.5708rad)
  Radius = 8.46154
FEATURE [Part::Cut] difference120
  Base = -> cube241
  Tool = -> cylinder172
FEATURE [Part::Box] cube242
  Height = 6.15385
  Length = 7.69231
  Placement = pos=(0,-0.5,9) rot=(0,0,1;0rad)
  Width = 45.9
FEATURE [Part::Cylinder] cylinder173
  Angle = 360
  Height = 45.9
  Placement = pos=(7.69231,45.4,11.5385) rot=(1,0,0;1.5708rad)
  Radius = 8.46154
FEATURE [Part::Cut] difference121
  Base = -> cube242
  Tool = -> cylinder173
FEATURE [Part::MultiFuse] union146
  Shapes = -> [union145,difference120,difference121]
FEATURE [Part::Cut] difference122
  Base = -> union144
  Tool = -> union146
FEATURE [Part::Cylinder] cylinder174
  Angle = 360
  Height = 44.2
  Placement = pos=(6.92308,44.7,10) rot=(1,0,0;1.5708rad)
  Radius = 2.84615
FEATURE [Part::Box] cube243
  Height = 4
  Length = 4
  Placement = pos=(0.538462,-2,6.92308) rot=(0,0,-1;0.349066rad)
  Width = 4
FEATURE [Part::Box] cube244
  Height = 4
  Length = 4
  Placement = pos=(0.538462,18.8,6.92308) rot=(0,0,-1;1.22173rad)
  Width = 4
FEATURE [Part::Fuse] union147
  Base = -> cube243
  Tool = -> cube244
FEATURE [Part::Cut] difference123
  Base = -> cylinder174
  Tool = -> union147
FEATURE [Part::Fuse] union148
  Base = -> difference122
  Tool = -> difference123
FEATURE [Part::Box] cube245
  Height = 17
  Length = 40
  Placement = pos=(-1.53846,3.4,1.5) rot=(0,0,1;0rad)
  Width = 38.4
FEATURE [Part::Box] cube246
  Height = 15.3846
  Length = 12.3077
  Placement = pos=(23.6154,3.4,5.38462) rot=(0,0,1;0rad)
  Width = 38.4
FEATURE [Part::Box] cube247
  Height = 24.6154
  Length = 12.3077
  Placement = pos=(-1.53846,3.4,-2.30769) rot=(0,0,1;0rad)
  Width = 38.4
FEATURE [Part::Box] cube248
  Height = 17
  Length = 9.23077
  Placement = pos=(19.2308,1.6,1.5) rot=(0,0,1;0rad)
  Width = 42
FEATURE [Part::Box] cube249
  Height = 20
  Length = 15.3846
  Placement = pos=(23.6154,1.6,0) rot=(0,0,1;0rad)
  Width = 42
FEATURE [Part::MultiFuse] Group024
  Shapes = -> [cube247,cube248,cube249]
FEATURE [Part::MultiFuse] union149
  Shapes = -> [cube245,cube246,Group024]
FEATURE [Part::Cut] difference124
  Base = -> union148
  Placement = pos=(395.551,234.896,566) rot=(-0.697457,-0.506732,0.506732;1.92356rad)
  Tool = -> union149
FEATURE [Part::Box] cube250
  Height = 20
  Length = 26.9231
  Placement = pos=(0,0.1,0) rot=(0,0,1;0rad)
  Width = 45
FEATURE [Part::Cylinder] cylinder175
  Angle = 360
  Height = 45
  Placement = pos=(26.9231,0.1,10) rot=(-1,0,0;1.5708rad)
  Radius = 10
FEATURE [Part::Fuse] union150
  Base = -> cube250
  Tool = -> cylinder175
FEATURE [Part::Cylinder] cylinder176
  Angle = 360
  Height = 3
  Placement = pos=(7.07692,2,10) rot=(1,0,0;1.5708rad)
  Radius = 10.5385
FEATURE [Part::Cylinder] cylinder177
  Angle = 360
  Height = 45.9
  Placement = pos=(29.2308,45.5,10) rot=(1,0,0;1.5708rad)
  Radius = 3.76923
FEATURE [Part::Cylinder] cylinder178
  Angle = 360
  Height = 3
  Placement = pos=(7.07692,46.3,10) rot=(1,0,0;1.5708rad)
  Radius = 10.5385
FEATURE [Part::MultiFuse] union151
  Shapes = -> [cylinder176,cylinder177,cylinder178]
FEATURE [Part::Box] cube251
  Height = 6.15385
  Length = 7.69231
  Placement = pos=(0,-0.5,0) rot=(0,0,1;0rad)
  Width = 45.9
FEATURE [Part::Cylinder] cylinder179
  Angle = 360
  Height = 45.9
  Placement = pos=(7.69231,45.4,8.46154) rot=(1,0,0;1.5708rad)
  Radius = 8.46154
FEATURE [Part::Cut] difference125
  Base = -> cube251
  Tool = -> cylinder179
FEATURE [Part::Box] cube252
  Height = 6.15385
  Length = 7.69231
  Placement = pos=(0,-0.5,9) rot=(0,0,1;0rad)
  Width = 45.9
FEATURE [Part::Cylinder] cylinder180
  Angle = 360
  Height = 45.9
  Placement = pos=(7.69231,45.4,11.5385) rot=(1,0,0;1.5708rad)
  Radius = 8.46154
FEATURE [Part::Cut] difference126
  Base = -> cube252
  Tool = -> cylinder180
FEATURE [Part::MultiFuse] union152
  Shapes = -> [union151,difference125,difference126]
FEATURE [Part::Cut] difference127
  Base = -> union150
  Tool = -> union152
FEATURE [Part::Cylinder] cylinder181
  Angle = 360
  Height = 44.2
  Placement = pos=(6.92308,44.7,10) rot=(1,0,0;1.5708rad)
  Radius = 2.84615
FEATURE [Part::Box] cube253
  Height = 4
  Length = 4
  Placement = pos=(0.538462,-2,6.92308) rot=(0,0,-1;0.349066rad)
  Width = 4
FEATURE [Part::Box] cube254
  Height = 4
  Length = 4
  Placement = pos=(0.538462,18.8,6.92308) rot=(0,0,-1;1.22173rad)
  Width = 4
FEATURE [Part::Fuse] union153
  Base = -> cube253
  Tool = -> cube254
FEATURE [Part::Cut] difference128
  Base = -> cylinder181
  Tool = -> union153
FEATURE [Part::Fuse] union154
  Base = -> difference127
  Tool = -> difference128
FEATURE [Part::Box] cube255
  Height = 17
  Length = 40
  Placement = pos=(-1.53846,3.4,1.5) rot=(0,0,1;0rad)
  Width = 38.4
FEATURE [Part::Box] cube256
  Height = 15.3846
  Length = 12.3077
  Placement = pos=(23.6154,3.4,5.38462) rot=(0,0,1;0rad)
  Width = 38.4
FEATURE [Part::Box] cube257
  Height = 24.6154
  Length = 12.3077
  Placement = pos=(-1.53846,3.4,-2.30769) rot=(0,0,1;0rad)
  Width = 38.4
FEATURE [Part::Box] cube258
  Height = 17
  Length = 9.23077
  Placement = pos=(19.2308,1.6,1.5) rot=(0,0,1;0rad)
  Width = 42
FEATURE [Part::Box] cube259
  Height = 20
  Length = 15.3846
  Placement = pos=(23.6154,1.6,0) rot=(0,0,1;0rad)
  Width = 42
FEATURE [Part::MultiFuse] Group025
  Shapes = -> [cube257,cube258,cube259]
FEATURE [Part::MultiFuse] union155
  Shapes = -> [cube255,cube256,Group025]
FEATURE [Part::Cut] difference129
  Base = -> union154
  Placement = pos=(403.102,256.649,566) rot=(-0.671033,-0.524268,0.524268;1.95955rad)
  Tool = -> union155
FEATURE [Part::Box] cube260
  Height = 20
  Length = 26.9231
  Placement = pos=(0,0.1,0) rot=(0,0,1;0rad)
  Width = 45
FEATURE [Part::Cylinder] cylinder182
  Angle = 360
  Height = 45
  Placement = pos=(26.9231,0.1,10) rot=(-1,0,0;1.5708rad)
  Radius = 10
FEATURE [Part::Fuse] union156
  Base = -> cube260
  Tool = -> cylinder182
FEATURE [Part::Cylinder] cylinder183
  Angle = 360
  Height = 3
  Placement = pos=(7.07692,2,10) rot=(1,0,0;1.5708rad)
  Radius = 10.5385
FEATURE [Part::Cylinder] cylinder184
  Angle = 360
  Height = 45.9
  Placement = pos=(29.2308,45.5,10) rot=(1,0,0;1.5708rad)
  Radius = 3.76923
FEATURE [Part::Cylinder] cylinder185
  Angle = 360
  Height = 3
  Placement = pos=(7.07692,46.3,10) rot=(1,0,0;1.5708rad)
  Radius = 10.5385
FEATURE [Part::MultiFuse] union157
  Shapes = -> [cylinder183,cylinder184,cylinder185]
FEATURE [Part::Box] cube261
  Height = 6.15385
  Length = 7.69231
  Placement = pos=(0,-0.5,0) rot=(0,0,1;0rad)
  Width = 45.9
FEATURE [Part::Cylinder] cylinder186
  Angle = 360
  Height = 45.9
  Placement = pos=(7.69231,45.4,8.46154) rot=(1,0,0;1.5708rad)
  Radius = 8.46154
FEATURE [Part::Cut] difference130
  Base = -> cube261
  Tool = -> cylinder186
FEATURE [Part::Box] cube262
  Height = 6.15385
  Length = 7.69231
  Placement = pos=(0,-0.5,9) rot=(0,0,1;0rad)
  Width = 45.9
FEATURE [Part::Cylinder] cylinder187
  Angle = 360
  Height = 45.9
  Placement = pos=(7.69231,45.4,11.5385) rot=(1,0,0;1.5708rad)
  Radius = 8.46154
FEATURE [Part::Cut] difference131
  Base = -> cube262
  Tool = -> cylinder187
FEATURE [Part::MultiFuse] union158
  Shapes = -> [union157,difference130,difference131]
FEATURE [Part::Cut] difference132
  Base = -> union156
  Tool = -> union158
FEATURE [Part::Cylinder] cylinder188
  Angle = 360
  Height = 44.2
  Placement = pos=(6.92308,44.7,10) rot=(1,0,0;1.5708rad)
  Radius = 2.84615
FEATURE [Part::Box] cube263
  Height = 4
  Length = 4
  Placement = pos=(0.538462,-2,6.92308) rot=(0,0,-1;0.349066rad)
  Width = 4
FEATURE [Part::Box] cube264
  Height = 4
  Length = 4
  Placement = pos=(0.538462,18.8,6.92308) rot=(0,0,-1;1.22173rad)
  Width = 4
FEATURE [Part::Fuse] union159
  Base = -> cube263
  Tool = -> cube264
FEATURE [Part::Cut] difference133
  Base = -> cylinder188
  Tool = -> union159
FEATURE [Part::Fuse] union160
  Base = -> difference132
  Tool = -> difference133
FEATURE [Part::Box] cube265
  Height = 17
  Length = 40
  Placement = pos=(-1.53846,3.4,1.5) rot=(0,0,1;0rad)
  Width = 38.4
FEATURE [Part::Box] cube266
  Height = 15.3846
  Length = 12.3077
  Placement = pos=(23.6154,3.4,5.38462) rot=(0,0,1;0rad)
  Width = 38.4
FEATURE [Part::Box] cube267
  Height = 24.6154
  Length = 12.3077
  Placement = pos=(-1.53846,3.4,-2.30769) rot=(0,0,1;0rad)
  Width = 38.4
FEATURE [Part::Box] cube268
  Height = 17
  Length = 9.23077
  Placement = pos=(19.2308,1.6,1.5) rot=(0,0,1;0rad)
  Width = 42
FEATURE [Part::Box] cube269
  Height = 20
  Length = 15.3846
  Placement = pos=(23.6154,1.6,0) rot=(0,0,1;0rad)
  Width = 42
FEATURE [Part::MultiFuse] Group026
  Shapes = -> [cube267,cube268,cube269]
FEATURE [Part::MultiFuse] union161
  Shapes = -> [cube265,cube266,Group026]
FEATURE [Part::Cut] difference134
  Base = -> union160
  Placement = pos=(409.117,278.876,566) rot=(-0.6444,-0.540716,0.540716;1.99673rad)
  Tool = -> union161
FEATURE [Part::Box] cube270
  Height = 20
  Length = 26.9231
  Placement = pos=(0,0.1,0) rot=(0,0,1;0rad)
  Width = 45
FEATURE [Part::Cylinder] cylinder189
  Angle = 360
  Height = 45
  Placement = pos=(26.9231,0.1,10) rot=(-1,0,0;1.5708rad)
  Radius = 10
FEATURE [Part::Fuse] union162
  Base = -> cube270
  Tool = -> cylinder189
FEATURE [Part::Cylinder] cylinder190
  Angle = 360
  Height = 3
  Placement = pos=(7.07692,2,10) rot=(1,0,0;1.5708rad)
  Radius = 10.5385
FEATURE [Part::Cylinder] cylinder191
  Angle = 360
  Height = 45.9
  Placement = pos=(29.2308,45.5,10) rot=(1,0,0;1.5708rad)
  Radius = 3.76923
FEATURE [Part::Cylinder] cylinder192
  Angle = 360
  Height = 3
  Placement = pos=(7.07692,46.3,10) rot=(1,0,0;1.5708rad)
  Radius = 10.5385
FEATURE [Part::MultiFuse] union163
  Shapes = -> [cylinder190,cylinder191,cylinder192]
FEATURE [Part::Box] cube271
  Height = 6.15385
  Length = 7.69231
  Placement = pos=(0,-0.5,0) rot=(0,0,1;0rad)
  Width = 45.9
FEATURE [Part::Cylinder] cylinder193
  Angle = 360
  Height = 45.9
  Placement = pos=(7.69231,45.4,8.46154) rot=(1,0,0;1.5708rad)
  Radius = 8.46154
FEATURE [Part::Cut] difference135
  Base = -> cube271
  Tool = -> cylinder193
FEATURE [Part::Box] cube272
  Height = 6.15385
  Length = 7.69231
  Placement = pos=(0,-0.5,9) rot=(0,0,1;0rad)
  Width = 45.9
FEATURE [Part::Cylinder] cylinder194
  Angle = 360
  Height = 45.9
  Placement = pos=(7.69231,45.4,11.5385) rot=(1,0,0;1.5708rad)
  Radius = 8.46154
FEATURE [Part::Cut] difference136
  Base = -> cube272
  Tool = -> cylinder194
FEATURE [Part::MultiFuse] union164
  Shapes = -> [union163,difference135,difference136]
FEATURE [Part::Cut] difference137
  Base = -> union162
  Tool = -> union164
FEATURE [Part::Cylinder] cylinder195
  Angle = 360
  Height = 44.2
  Placement = pos=(6.92308,44.7,10) rot=(1,0,0;1.5708rad)
  Radius = 2.84615
FEATURE [Part::Box] cube273
  Height = 4
  Length = 4
  Placement = pos=(0.538462,-2,6.92308) rot=(0,0,-1;0.349066rad)
  Width = 4
FEATURE [Part::Box] cube274
  Height = 4
  Length = 4
  Placement = pos=(0.538462,18.8,6.92308) rot=(0,0,-1;1.22173rad)
  Width = 4
FEATURE [Part::Fuse] union165
  Base = -> cube273
  Tool = -> cube274
FEATURE [Part::Cut] difference138
  Base = -> cylinder195
  Tool = -> union165
FEATURE [Part::Fuse] union166
  Base = -> difference137
  Tool = -> difference138
FEATURE [Part::Box] cube275
  Height = 17
  Length = 40
  Placement = pos=(-1.53846,3.4,1.5) rot=(0,0,1;0rad)
  Width = 38.4
FEATURE [Part::Box] cube276
  Height = 15.3846
  Length = 12.3077
  Placement = pos=(23.6154,3.4,5.38462) rot=(0,0,1;0rad)
  Width = 38.4
FEATURE [Part::Box] cube277
  Height = 24.6154
  Length = 12.3077
  Placement = pos=(-1.53846,3.4,-2.30769) rot=(0,0,1;0rad)
  Width = 38.4
FEATURE [Part::Box] cube278
  Height = 17
  Length = 9.23077
  Placement = pos=(19.2308,1.6,1.5) rot=(0,0,1;0rad)
  Width = 42
FEATURE [Part::Box] cube279
  Height = 20
  Length = 15.3846
  Placement = pos=(23.6154,1.6,0) rot=(0,0,1;0rad)
  Width = 42
FEATURE [Part::MultiFuse] Group027
  Shapes = -> [cube277,cube278,cube279]
FEATURE [Part::MultiFuse] union167
  Shapes = -> [cube275,cube276,Group027]
FEATURE [Part::Cut] difference139
  Base = -> union166
  Placement = pos=(413.565,301.469,566) rot=(-0.617631,-0.556117,0.556117;2.03503rad)
  Tool = -> union167
FEATURE [Part::Box] cube280
  Height = 20
  Length = 26.9231
  Placement = pos=(0,0.1,0) rot=(0,0,1;0rad)
  Width = 45
FEATURE [Part::Cylinder] cylinder196
  Angle = 360
  Height = 45
  Placement = pos=(26.9231,0.1,10) rot=(-1,0,0;1.5708rad)
  Radius = 10
FEATURE [Part::Fuse] union168
  Base = -> cube280
  Tool = -> cylinder196
FEATURE [Part::Cylinder] cylinder197
  Angle = 360
  Height = 3
  Placement = pos=(7.07692,2,10) rot=(1,0,0;1.5708rad)
  Radius = 10.5385
FEATURE [Part::Cylinder] cylinder198
  Angle = 360
  Height = 45.9
  Placement = pos=(29.2308,45.5,10) rot=(1,0,0;1.5708rad)
  Radius = 3.76923
FEATURE [Part::Cylinder] cylinder199
  Angle = 360
  Height = 3
  Placement = pos=(7.07692,46.3,10) rot=(1,0,0;1.5708rad)
  Radius = 10.5385
FEATURE [Part::MultiFuse] union169
  Shapes = -> [cylinder197,cylinder198,cylinder199]
FEATURE [Part::Box] cube281
  Height = 6.15385
  Length = 7.69231
  Placement = pos=(0,-0.5,0) rot=(0,0,1;0rad)
  Width = 45.9
FEATURE [Part::Cylinder] cylinder200
  Angle = 360
  Height = 45.9
  Placement = pos=(7.69231,45.4,8.46154) rot=(1,0,0;1.5708rad)
  Radius = 8.46154
FEATURE [Part::Cut] difference140
  Base = -> cube281
  Tool = -> cylinder200
FEATURE [Part::Box] cube282
  Height = 6.15385
  Length = 7.69231
  Placement = pos=(0,-0.5,9) rot=(0,0,1;0rad)
  Width = 45.9
FEATURE [Part::Cylinder] cylinder201
  Angle = 360
  Height = 45.9
  Placement = pos=(7.69231,45.4,11.5385) rot=(1,0,0;1.5708rad)
  Radius = 8.46154
FEATURE [Part::Cut] difference141
  Base = -> cube282
  Tool = -> cylinder201
FEATURE [Part::MultiFuse] union170
  Shapes = -> [union169,difference140,difference141]
FEATURE [Part::Cut] difference142
  Base = -> union168
  Tool = -> union170
FEATURE [Part::Cylinder] cylinder202
  Angle = 360
  Height = 44.2
  Placement = pos=(6.92308,44.7,10) rot=(1,0,0;1.5708rad)
  Radius = 2.84615
FEATURE [Part::Box] cube283
  Height = 4
  Length = 4
  Placement = pos=(0.538462,-2,6.92308) rot=(0,0,-1;0.349066rad)
  Width = 4
FEATURE [Part::Box] cube284
  Height = 4
  Length = 4
  Placement = pos=(0.538462,18.8,6.92308) rot=(0,0,-1;1.22173rad)
  Width = 4
FEATURE [Part::Fuse] union171
  Base = -> cube283
  Tool = -> cube284
FEATURE [Part::Cut] difference143
  Base = -> cylinder202
  Tool = -> union171
FEATURE [Part::Fuse] union172
  Base = -> difference142
  Tool = -> difference143
FEATURE [Part::Box] cube285
  Height = 17
  Length = 40
  Placement = pos=(-1.53846,3.4,1.5) rot=(0,0,1;0rad)
  Width = 38.4
FEATURE [Part::Box] cube286
  Height = 15.3846
  Length = 12.3077
  Placement = pos=(23.6154,3.4,5.38462) rot=(0,0,1;0rad)
  Width = 38.4
FEATURE [Part::Box] cube287
  Height = 24.6154
  Length = 12.3077
  Placement = pos=(-1.53846,3.4,-2.30769) rot=(0,0,1;0rad)
  Width = 38.4
FEATURE [Part::Box] cube288
  Height = 17
  Length = 9.23077
  Placement = pos=(19.2308,1.6,1.5) rot=(0,0,1;0rad)
  Width = 42
FEATURE [Part::Box] cube289
  Height = 20
  Length = 15.3846
  Placement = pos=(23.6154,1.6,0) rot=(0,0,1;0rad)
  Width = 42
FEATURE [Part::MultiFuse] Group028
  Shapes = -> [cube287,cube288,cube289]
FEATURE [Part::MultiFuse] union173
  Shapes = -> [cube285,cube286,Group028]
FEATURE [Part::Cut] difference144
  Base = -> union172
  Placement = pos=(416.3,324.148,566) rot=(-0.5975,-0.567007,0.567007;2.06443rad)
  Tool = -> union173
FEATURE [Part::Box] cube290
  Height = 20
  Length = 26.9231
  Placement = pos=(0,0.1,0) rot=(0,0,1;0rad)
  Width = 45
FEATURE [Part::Cylinder] cylinder203
  Angle = 360
  Height = 45
  Placement = pos=(26.9231,0.1,10) rot=(-1,0,0;1.5708rad)
  Radius = 10
FEATURE [Part::Fuse] union174
  Base = -> cube290
  Tool = -> cylinder203
FEATURE [Part::Cylinder] cylinder204
  Angle = 360
  Height = 3
  Placement = pos=(7.07692,2,10) rot=(1,0,0;1.5708rad)
  Radius = 10.5385
FEATURE [Part::Cylinder] cylinder205
  Angle = 360
  Height = 45.9
  Placement = pos=(29.2308,45.5,10) rot=(1,0,0;1.5708rad)
  Radius = 3.76923
FEATURE [Part::Cylinder] cylinder206
  Angle = 360
  Height = 3
  Placement = pos=(7.07692,46.3,10) rot=(1,0,0;1.5708rad)
  Radius = 10.5385
FEATURE [Part::MultiFuse] union175
  Shapes = -> [cylinder204,cylinder205,cylinder206]
FEATURE [Part::Box] cube291
  Height = 6.15385
  Length = 7.69231
  Placement = pos=(0,-0.5,0) rot=(0,0,1;0rad)
  Width = 45.9
FEATURE [Part::Cylinder] cylinder207
  Angle = 360
  Height = 45.9
  Placement = pos=(7.69231,45.4,8.46154) rot=(1,0,0;1.5708rad)
  Radius = 8.46154
FEATURE [Part::Cut] difference145
  Base = -> cube291
  Tool = -> cylinder207
FEATURE [Part::Box] cube292
  Height = 6.15385
  Length = 7.69231
  Placement = pos=(0,-0.5,9) rot=(0,0,1;0rad)
  Width = 45.9
FEATURE [Part::Cylinder] cylinder208
  Angle = 360
  Height = 45.9
  Placement = pos=(7.69231,45.4,11.5385) rot=(1,0,0;1.5708rad)
  Radius = 8.46154
FEATURE [Part::Cut] difference146
  Base = -> cube292
  Tool = -> cylinder208
FEATURE [Part::MultiFuse] union176
  Shapes = -> [union175,difference145,difference146]
FEATURE [Part::Cut] difference147
  Base = -> union174
  Tool = -> union176
FEATURE [Part::Cylinder] cylinder209
  Angle = 360
  Height = 44.2
  Placement = pos=(6.92308,44.7,10) rot=(1,0,0;1.5708rad)
  Radius = 2.84615
FEATURE [Part::Box] cube293
  Height = 4
  Length = 4
  Placement = pos=(0.538462,-2,6.92308) rot=(0,0,-1;0.349066rad)
  Width = 4
FEATURE [Part::Box] cube294
  Height = 4
  Length = 4
  Placement = pos=(0.538462,18.8,6.92308) rot=(0,0,-1;1.22173rad)
  Width = 4
FEATURE [Part::Fuse] union177
  Base = -> cube293
  Tool = -> cube294
FEATURE [Part::Cut] difference148
  Base = -> cylinder209
  Tool = -> union177
FEATURE [Part::Fuse] union178
  Base = -> difference147
  Tool = -> difference148
FEATURE [Part::Box] cube295
  Height = 17
  Length = 40
  Placement = pos=(-1.53846,3.4,1.5) rot=(0,0,1;0rad)
  Width = 38.4
FEATURE [Part::Box] cube296
  Height = 15.3846
  Length = 12.3077
  Placement = pos=(23.6154,3.4,5.38462) rot=(0,0,1;0rad)
  Width = 38.4
FEATURE [Part::Box] cube297
  Height = 24.6154
  Length = 12.3077
  Placement = pos=(-1.53846,3.4,-2.30769) rot=(0,0,1;0rad)
  Width = 38.4
FEATURE [Part::Box] cube298
  Height = 17
  Length = 9.23077
  Placement = pos=(19.2308,1.6,1.5) rot=(0,0,1;0rad)
  Width = 42
FEATURE [Part::Box] cube299
  Height = 20
  Length = 15.3846
  Placement = pos=(23.6154,1.6,0) rot=(0,0,1;0rad)
  Width = 42
FEATURE [Part::MultiFuse] Group029
  Shapes = -> [cube297,cube298,cube299]
FEATURE [Part::MultiFuse] union179
  Shapes = -> [cube295,cube296,Group029]
FEATURE [Part::Cut] difference149
  Base = -> union178
  Placement = pos=(417.844,346.939,566) rot=(-0.57735,-0.57735,0.57735;2.0944rad)
  Tool = -> union179
FEATURE [Part::Box] cube300
  Height = 20
  Length = 26.9231
  Placement = pos=(0,0.1,0) rot=(0,0,1;0rad)
  Width = 45
FEATURE [Part::Cylinder] cylinder210
  Angle = 360
  Height = 45
  Placement = pos=(26.9231,0.1,10) rot=(-1,0,0;1.5708rad)
  Radius = 10
FEATURE [Part::Fuse] union180
  Base = -> cube300
  Tool = -> cylinder210
FEATURE [Part::Cylinder] cylinder211
  Angle = 360
  Height = 3
  Placement = pos=(7.07692,2,10) rot=(1,0,0;1.5708rad)
  Radius = 10.5385
FEATURE [Part::Cylinder] cylinder212
  Angle = 360
  Height = 45.9
  Placement = pos=(29.2308,45.5,10) rot=(1,0,0;1.5708rad)
  Radius = 3.76923
FEATURE [Part::Cylinder] cylinder213
  Angle = 360
  Height = 3
  Placement = pos=(7.07692,46.3,10) rot=(1,0,0;1.5708rad)
  Radius = 10.5385
FEATURE [Part::MultiFuse] union181
  Shapes = -> [cylinder211,cylinder212,cylinder213]
FEATURE [Part::Box] cube301
  Height = 6.15385
  Length = 7.69231
  Placement = pos=(0,-0.5,0) rot=(0,0,1;0rad)
  Width = 45.9
FEATURE [Part::Cylinder] cylinder214
  Angle = 360
  Height = 45.9
  Placement = pos=(7.69231,45.4,8.46154) rot=(1,0,0;1.5708rad)
  Radius = 8.46154
FEATURE [Part::Cut] difference150
  Base = -> cube301
  Tool = -> cylinder214
FEATURE [Part::Box] cube302
  Height = 6.15385
  Length = 7.69231
  Placement = pos=(0,-0.5,9) rot=(0,0,1;0rad)
  Width = 45.9
FEATURE [Part::Cylinder] cylinder215
  Angle = 360
  Height = 45.9
  Placement = pos=(7.69231,45.4,11.5385) rot=(1,0,0;1.5708rad)
  Radius = 8.46154
FEATURE [Part::Cut] difference151
  Base = -> cube302
  Tool = -> cylinder215
FEATURE [Part::MultiFuse] union182
  Shapes = -> [union181,difference150,difference151]
FEATURE [Part::Cut] difference152
  Base = -> union180
  Tool = -> union182
FEATURE [Part::Cylinder] cylinder216
  Angle = 360
  Height = 44.2
  Placement = pos=(6.92308,44.7,10) rot=(1,0,0;1.5708rad)
  Radius = 2.84615
FEATURE [Part::Box] cube303
  Height = 4
  Length = 4
  Placement = pos=(0.538462,-2,6.92308) rot=(0,0,-1;0.349066rad)
  Width = 4
FEATURE [Part::Box] cube304
  Height = 4
  Length = 4
  Placement = pos=(0.538462,18.8,6.92308) rot=(0,0,-1;1.22173rad)
  Width = 4
FEATURE [Part::Fuse] union183
  Base = -> cube303
  Tool = -> cube304
FEATURE [Part::Cut] difference153
  Base = -> cylinder216
  Tool = -> union183
FEATURE [Part::Fuse] union184
  Base = -> difference152
  Tool = -> difference153
FEATURE [Part::Box] cube305
  Height = 17
  Length = 40
  Placement = pos=(-1.53846,3.4,1.5) rot=(0,0,1;0rad)
  Width = 38.4
FEATURE [Part::Box] cube306
  Height = 15.3846
  Length = 12.3077
  Placement = pos=(23.6154,3.4,5.38462) rot=(0,0,1;0rad)
  Width = 38.4
FEATURE [Part::Box] cube307
  Height = 24.6154
  Length = 12.3077
  Placement = pos=(-1.53846,3.4,-2.30769) rot=(0,0,1;0rad)
  Width = 38.4
FEATURE [Part::Box] cube308
  Height = 17
  Length = 9.23077
  Placement = pos=(19.2308,1.6,1.5) rot=(0,0,1;0rad)
  Width = 42
FEATURE [Part::Box] cube309
  Height = 20
  Length = 15.3846
  Placement = pos=(23.6154,1.6,0) rot=(0,0,1;0rad)
  Width = 42
FEATURE [Part::MultiFuse] Group030
  Shapes = -> [cube307,cube308,cube309]
FEATURE [Part::MultiFuse] union185
  Shapes = -> [cube305,cube306,Group030]
FEATURE [Part::Cut] difference154
  Base = -> union184
  Placement = pos=(417.844,369.247,566) rot=(-0.57735,-0.57735,0.57735;2.0944rad)
  Tool = -> union185
FEATURE [Part::Box] cube310
  Height = 20
  Length = 26.9231
  Placement = pos=(0,0.1,0) rot=(0,0,1;0rad)
  Width = 45
FEATURE [Part::Cylinder] cylinder217
  Angle = 360
  Height = 45
  Placement = pos=(26.9231,0.1,10) rot=(-1,0,0;1.5708rad)
  Radius = 10
FEATURE [Part::Fuse] union186
  Base = -> cube310
  Tool = -> cylinder217
FEATURE [Part::Cylinder] cylinder218
  Angle = 360
  Height = 3
  Placement = pos=(7.07692,2,10) rot=(1,0,0;1.5708rad)
  Radius = 10.5385
FEATURE [Part::Cylinder] cylinder219
  Angle = 360
  Height = 45.9
  Placement = pos=(29.2308,45.5,10) rot=(1,0,0;1.5708rad)
  Radius = 3.76923
FEATURE [Part::Cylinder] cylinder220
  Angle = 360
  Height = 3
  Placement = pos=(7.07692,46.3,10) rot=(1,0,0;1.5708rad)
  Radius = 10.5385
FEATURE [Part::MultiFuse] union187
  Shapes = -> [cylinder218,cylinder219,cylinder220]
FEATURE [Part::Box] cube311
  Height = 6.15385
  Length = 7.69231
  Placement = pos=(0,-0.5,0) rot=(0,0,1;0rad)
  Width = 45.9
FEATURE [Part::Cylinder] cylinder221
  Angle = 360
  Height = 45.9
  Placement = pos=(7.69231,45.4,8.46154) rot=(1,0,0;1.5708rad)
  Radius = 8.46154
FEATURE [Part::Cut] difference155
  Base = -> cube311
  Tool = -> cylinder221
FEATURE [Part::Box] cube312
  Height = 6.15385
  Length = 7.69231
  Placement = pos=(0,-0.5,9) rot=(0,0,1;0rad)
  Width = 45.9
FEATURE [Part::Cylinder] cylinder222
  Angle = 360
  Height = 45.9
  Placement = pos=(7.69231,45.4,11.5385) rot=(1,0,0;1.5708rad)
  Radius = 8.46154
FEATURE [Part::Cut] difference156
  Base = -> cube312
  Tool = -> cylinder222
FEATURE [Part::MultiFuse] union188
  Shapes = -> [union187,difference155,difference156]
FEATURE [Part::Cut] difference157
  Base = -> union186
  Tool = -> union188
FEATURE [Part::Cylinder] cylinder223
  Angle = 360
  Height = 44.2
  Placement = pos=(6.92308,44.7,10) rot=(1,0,0;1.5708rad)
  Radius = 2.84615
FEATURE [Part::Box] cube313
  Height = 4
  Length = 4
  Placement = pos=(0.538462,-2,6.92308) rot=(0,0,-1;0.349066rad)
  Width = 4
FEATURE [Part::Box] cube314
  Height = 4
  Length = 4
  Placement = pos=(0.538462,18.8,6.92308) rot=(0,0,-1;1.22173rad)
  Width = 4
FEATURE [Part::Fuse] union189
  Base = -> cube313
  Tool = -> cube314
FEATURE [Part::Cut] difference158
  Base = -> cylinder223
  Tool = -> union189
FEATURE [Part::Fuse] union190
  Base = -> difference157
  Tool = -> difference158
FEATURE [Part::Box] cube315
  Height = 17
  Length = 40
  Placement = pos=(-1.53846,3.4,1.5) rot=(0,0,1;0rad)
  Width = 38.4
FEATURE [Part::Box] cube316
  Height = 15.3846
  Length = 12.3077
  Placement = pos=(23.6154,3.4,5.38462) rot=(0,0,1;0rad)
  Width = 38.4
FEATURE [Part::Box] cube317
  Height = 24.6154
  Length = 12.3077
  Placement = pos=(-1.53846,3.4,-2.30769) rot=(0,0,1;0rad)
  Width = 38.4
FEATURE [Part::Box] cube318
  Height = 17
  Length = 9.23077
  Placement = pos=(19.2308,1.6,1.5) rot=(0,0,1;0rad)
  Width = 42
FEATURE [Part::Box] cube319
  Height = 20
  Length = 15.3846
  Placement = pos=(23.6154,1.6,0) rot=(0,0,1;0rad)
  Width = 42
FEATURE [Part::MultiFuse] Group031
  Shapes = -> [cube317,cube318,cube319]
FEATURE [Part::MultiFuse] union191
  Shapes = -> [cube315,cube316,Group031]
FEATURE [Part::Cut] difference159
  Base = -> union190
  Placement = pos=(417.844,391.555,566) rot=(-0.57735,-0.57735,0.57735;2.0944rad)
  Tool = -> union191
FEATURE [Part::MultiFuse] Group032
  Shapes = -> [difference004,difference009,difference014,difference019,difference024,difference029,difference034,difference039,difference044,difference049,difference054,difference059,difference064,difference069,difference074,difference079,difference084,difference089,difference094,difference099,difference104,difference109,difference114,difference119,difference124,difference129,difference134,difference139,+4 more]
FEATURE [Part::FeaturePython] refine  label="refine_Group032"  # WARN: FeaturePython — macro-defined, semantics opaque (R4)
  Base = -> Group032
